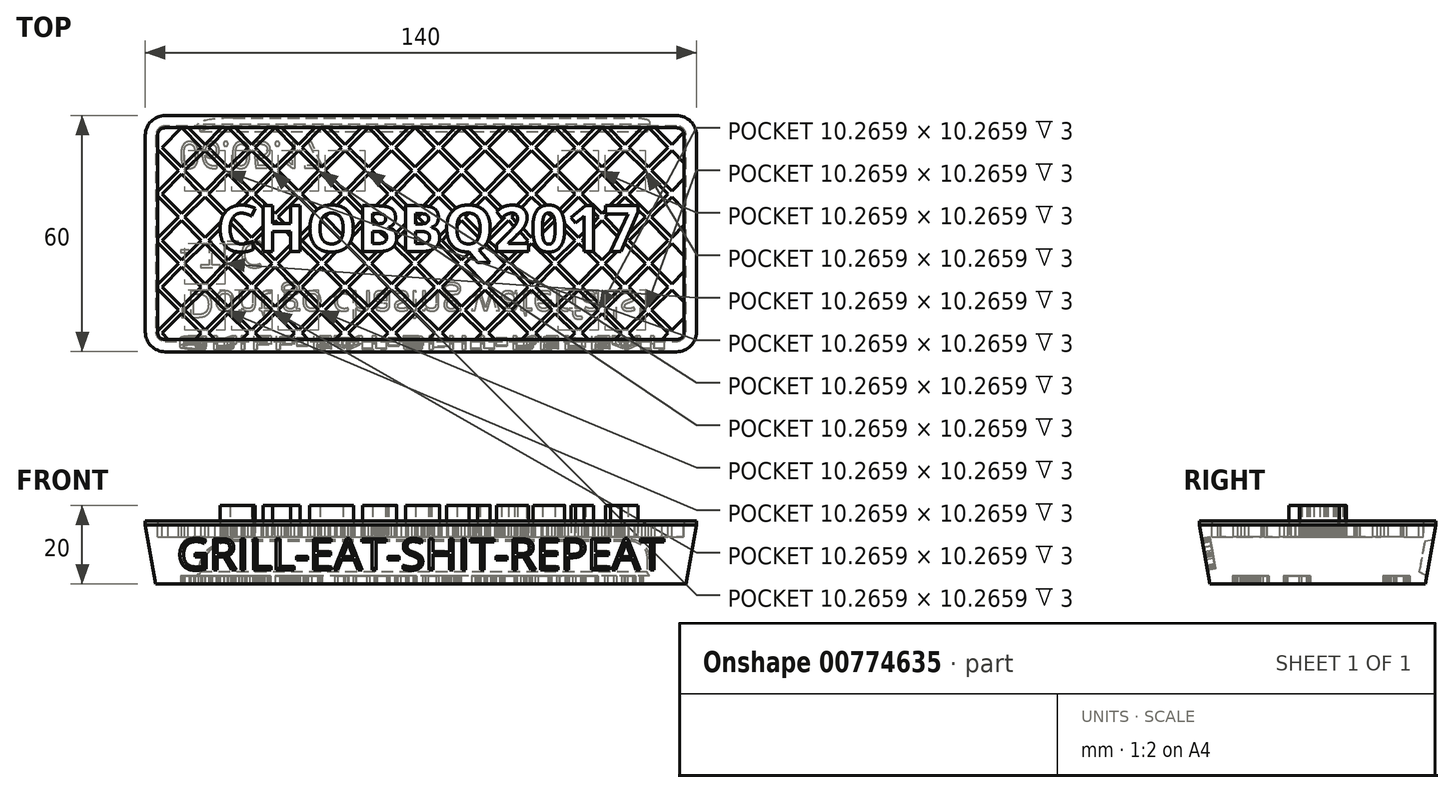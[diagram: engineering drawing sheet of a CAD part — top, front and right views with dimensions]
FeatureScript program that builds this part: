
annotation { "Feature Type Name" : "Feature", "Feature Type Description" : "" }
export const myFeature = defineFeature(function(context is Context, id is Id, definition is map)
    precondition{}
    {
        {
            var Q0;
            Q0=qCreatedBy(makeId("Top.planeOp"),FACE);
            var sketch = newSketch(context, id + "F0", { "sketchPlane" : qUnion([Q0])});
            skText(sketch, "E0", { "text": "CHOBBQ2017", "fontName": "NotoSans-Bold.ttf"});
            const initialGuessF0  = {"E0": [-0.0529, 0, 1, 0, 0.0117]};
            skSetInitialGuess(sketch, initialGuessF0);
            skSolve(sketch);
        }
        {
            var Q0;
            Q0=qCreatedBy(makeId("Top.planeOp"),FACE);
            var sketch = newSketch(context, id + "F1", { "sketchPlane" : qUnion([Q0])});
            skLineSegment(sketch, "E1.bottom", {"start": v(-65.96, 34.5) * mm, "end": v(64.04, 34.5) * mm});
            skLineSegment(sketch, "E1.top", {"start": v(-65.96, -25.5) * mm, "end": v(64.04, -25.5) * mm});
            skLineSegment(sketch, "E1.left", {"start": v(-70.96, 29.5) * mm, "end": v(-70.96, -20.5) * mm});
            skLineSegment(sketch, "E1.right", {"start": v(69.04, 29.5) * mm, "end": v(69.04, -20.5) * mm});
            skPoint(sketch, "E2.visualSharp", {"position": v(-70.96, 34.5) * mm});
            skArc(sketch, "E2.filletArc", {"start": v(-65.96, 34.5) * mm, "mid": v(-69.5, 33.04) * mm, "end": v(-70.96, 29.5) * mm});
            skPoint(sketch, "E3.visualSharp", {"position": v(-70.96, -25.5) * mm});
            skArc(sketch, "E3.filletArc", {"start": v(-70.96, -20.5) * mm, "mid": v(-69.5, -24.03) * mm, "end": v(-65.96, -25.5) * mm});
            skPoint(sketch, "E4.visualSharp", {"position": v(69.04, -25.5) * mm});
            skArc(sketch, "E4.filletArc", {"start": v(64.04, -25.5) * mm, "mid": v(67.58, -24.03) * mm, "end": v(69.04, -20.5) * mm});
            skPoint(sketch, "E5.visualSharp", {"position": v(69.04, 34.5) * mm});
            skArc(sketch, "E5.filletArc", {"start": v(69.04, 29.5) * mm, "mid": v(67.58, 33.04) * mm, "end": v(64.04, 34.5) * mm});
            skSolve(sketch);
        }
        {
            var Q0;
            Q0=makeQuery(id+"F1.imprint","IMPRINT",FACE,{"disambiguationData":[TD([[makeQuery(id+"F1.imprint","IMPRINT",EDGE,{"derivedFrom":sQuery(id+"F1.wireOp",EDGE,"E1.bottom")}),-1.0]])]});
            extrude(context, id + "F2", {"entities" : qUnion([Q0]), "oppositeDirection" : true, "depth" : 15 * mm, "offsetDistance" : 25 * mm, "hasDraft" : true, "draftAngle" : 10 * degree, "draftPullDirection" : true});
        }
        {
            var Q0;
            Q0=makeQuery(id+"F2.opExtrude","CAP_FACE",FACE,{"disambiguationData":[OSD([sQuery(id+"F1.wireOp",EDGE,"E1.bottom"),sQuery(id+"F1.wireOp",EDGE,"E1.top"),sQuery(id+"F1.wireOp",EDGE,"E1.left"),sQuery(id+"F1.wireOp",EDGE,"E1.right"),sQuery(id+"F1.wireOp",EDGE,"E2.filletArc"),sQuery(id+"F1.wireOp",EDGE,"E3.filletArc"),sQuery(id+"F1.wireOp",EDGE,"E4.filletArc"),sQuery(id+"F1.wireOp",EDGE,"E5.filletArc")])],"isStart":true});
            var sketch = newSketch(context, id + "F3", { "sketchPlane" : qUnion([Q0])});
            skArc(sketch, "E6.0", {"start": v(-65.96, 31.4) * mm, "mid": v(-67.3, 30.85) * mm, "end": v(-67.86, 29.5) * mm});
            skLineSegment(sketch, "E6.1", {"start": v(-67.86, 29.5) * mm, "end": v(-67.86, -20.5) * mm});
            skLineSegment(sketch, "E6.2", {"start": v(-65.96, 31.4) * mm, "end": v(64.04, 31.4) * mm});
            skArc(sketch, "E6.3", {"start": v(-67.86, -20.5) * mm, "mid": v(-67.3, -21.84) * mm, "end": v(-65.96, -22.4) * mm});
            skArc(sketch, "E6.4", {"start": v(65.94, 29.5) * mm, "mid": v(65.39, 30.85) * mm, "end": v(64.04, 31.4) * mm});
            skLineSegment(sketch, "E6.5", {"start": v(65.94, 29.5) * mm, "end": v(65.94, -20.5) * mm});
            skArc(sketch, "E6.6", {"start": v(64.04, -22.4) * mm, "mid": v(65.39, -21.84) * mm, "end": v(65.94, -20.5) * mm});
            skLineSegment(sketch, "E6.7", {"start": v(-65.96, -22.4) * mm, "end": v(64.04, -22.4) * mm});
            skSolve(sketch);
        }
        {
            var Q0;
            Q0=makeQuery(id+"F3.imprint","IMPRINT",FACE,{"disambiguationData":[TD([[makeQuery(id+"F3.imprint","IMPRINT",EDGE,{"derivedFrom":sQuery(id+"F3.wireOp",EDGE,"E6.0")}),-1.0]])]});
            extrude(context, id + "F4", {"entities" : qUnion([Q0]), "operationType" : NewBodyOperationType.ADD, "depth" : 1 * mm, "offsetDistance" : 25 * mm});
        }
        {
            var Q0;
            Q0=makeQuery(id+"F2.opExtrude","CAP_FACE",FACE,{"disambiguationData":[OSD([sQuery(id+"F1.wireOp",EDGE,"E1.bottom"),sQuery(id+"F1.wireOp",EDGE,"E1.top"),sQuery(id+"F1.wireOp",EDGE,"E1.left"),sQuery(id+"F1.wireOp",EDGE,"E1.right"),sQuery(id+"F1.wireOp",EDGE,"E2.filletArc"),sQuery(id+"F1.wireOp",EDGE,"E3.filletArc"),sQuery(id+"F1.wireOp",EDGE,"E4.filletArc"),sQuery(id+"F1.wireOp",EDGE,"E5.filletArc")])],"isStart":true});
            var sketch = newSketch(context, id + "F5", { "sketchPlane" : qUnion([Q0])});
            skLineSegment(sketch, "E7", {"start": v(-66.74, 26.4) * mm, "end": v(-61.74, 31.4) * mm});
            skLineSegment(sketch, "E8", {"start": v(-66.74, 26.4) * mm, "end": v(-61.74, 21.4) * mm});
            skLineSegment(sketch, "E9", {"start": v(-61.74, 21.4) * mm, "end": v(-56.74, 26.4) * mm});
            skLineSegment(sketch, "E10", {"start": v(-56.74, 26.4) * mm, "end": v(-61.74, 31.4) * mm});
            skLineSegment(sketch, "E11.0", {"start": v(-61.74, 19.7) * mm, "end": v(-55.04, 26.4) * mm});
            skLineSegment(sketch, "E11.1", {"start": v(-68.44, 26.4) * mm, "end": v(-61.74, 19.7) * mm});
            skLineSegment(sketch, "E11.2", {"start": v(-68.44, 26.4) * mm, "end": v(-61.74, 33.1) * mm});
            skLineSegment(sketch, "E11.3", {"start": v(-55.04, 26.4) * mm, "end": v(-61.74, 33.1) * mm});
            skLineSegment(sketch, "E12.0.1.0", {"start": v(-68.44, 14.6) * mm, "end": v(-61.74, 21.3) * mm});
            skLineSegment(sketch, "E12.0.1.1", {"start": v(-66.74, 14.6) * mm, "end": v(-61.74, 19.6) * mm});
            skLineSegment(sketch, "E12.0.1.2", {"start": v(-55.04, 14.6) * mm, "end": v(-61.74, 21.3) * mm});
            skLineSegment(sketch, "E12.0.1.3", {"start": v(-56.74, 14.6) * mm, "end": v(-61.74, 19.6) * mm});
            skLineSegment(sketch, "E12.0.1.4", {"start": v(-61.74, 7.9) * mm, "end": v(-55.04, 14.6) * mm});
            skLineSegment(sketch, "E12.0.1.5", {"start": v(-61.74, 9.6) * mm, "end": v(-56.74, 14.6) * mm});
            skLineSegment(sketch, "E12.0.1.6", {"start": v(-66.74, 14.6) * mm, "end": v(-61.74, 9.6) * mm});
            skLineSegment(sketch, "E12.0.1.7", {"start": v(-68.44, 14.6) * mm, "end": v(-61.74, 7.9) * mm});
            skLineSegment(sketch, "E12.0.2.0", {"start": v(-68.44, 2.8) * mm, "end": v(-61.74, 9.5) * mm});
            skLineSegment(sketch, "E12.0.2.1", {"start": v(-66.74, 2.8) * mm, "end": v(-61.74, 7.8) * mm});
            skLineSegment(sketch, "E12.0.2.2", {"start": v(-55.04, 2.8) * mm, "end": v(-61.74, 9.5) * mm});
            skLineSegment(sketch, "E12.0.2.3", {"start": v(-56.74, 2.8) * mm, "end": v(-61.74, 7.8) * mm});
            skLineSegment(sketch, "E12.0.2.4", {"start": v(-61.74, -3.9) * mm, "end": v(-55.04, 2.8) * mm});
            skLineSegment(sketch, "E12.0.2.5", {"start": v(-61.74, -2.2) * mm, "end": v(-56.74, 2.8) * mm});
            skLineSegment(sketch, "E12.0.2.6", {"start": v(-66.74, 2.8) * mm, "end": v(-61.74, -2.2) * mm});
            skLineSegment(sketch, "E12.0.2.7", {"start": v(-68.44, 2.8) * mm, "end": v(-61.74, -3.9) * mm});
            skLineSegment(sketch, "E12.0.3.0", {"start": v(-68.44, -9) * mm, "end": v(-61.74, -2.3) * mm});
            skLineSegment(sketch, "E12.0.3.1", {"start": v(-66.74, -9) * mm, "end": v(-61.74, -4) * mm});
            skLineSegment(sketch, "E12.0.3.2", {"start": v(-55.04, -9) * mm, "end": v(-61.74, -2.3) * mm});
            skLineSegment(sketch, "E12.0.3.3", {"start": v(-56.74, -9) * mm, "end": v(-61.74, -4) * mm});
            skLineSegment(sketch, "E12.0.3.4", {"start": v(-61.74, -15.7) * mm, "end": v(-55.04, -9) * mm});
            skLineSegment(sketch, "E12.0.3.5", {"start": v(-61.74, -14) * mm, "end": v(-56.74, -9) * mm});
            skLineSegment(sketch, "E12.0.3.6", {"start": v(-66.74, -9) * mm, "end": v(-61.74, -14) * mm});
            skLineSegment(sketch, "E12.0.3.7", {"start": v(-68.44, -9) * mm, "end": v(-61.74, -15.7) * mm});
            skLineSegment(sketch, "E12.0.4.0", {"start": v(-68.44, -20.8) * mm, "end": v(-61.74, -14.1) * mm});
            skLineSegment(sketch, "E12.0.4.1", {"start": v(-66.74, -20.8) * mm, "end": v(-61.74, -15.8) * mm});
            skLineSegment(sketch, "E12.0.4.2", {"start": v(-55.04, -20.8) * mm, "end": v(-61.74, -14.1) * mm});
            skLineSegment(sketch, "E12.0.4.3", {"start": v(-56.74, -20.8) * mm, "end": v(-61.74, -15.8) * mm});
            skLineSegment(sketch, "E12.0.4.4", {"start": v(-61.74, -27.5) * mm, "end": v(-55.04, -20.8) * mm});
            skLineSegment(sketch, "E12.0.4.5", {"start": v(-61.74, -25.8) * mm, "end": v(-56.74, -20.8) * mm});
            skLineSegment(sketch, "E12.0.4.6", {"start": v(-66.74, -20.8) * mm, "end": v(-61.74, -25.8) * mm});
            skLineSegment(sketch, "E12.0.4.7", {"start": v(-68.44, -20.8) * mm, "end": v(-61.74, -27.5) * mm});
            skLineSegment(sketch, "E12.1.0.0", {"start": v(-56.58, 26.4) * mm, "end": v(-49.88, 33.1) * mm});
            skLineSegment(sketch, "E12.1.0.1", {"start": v(-54.88, 26.4) * mm, "end": v(-49.88, 31.4) * mm});
            skLineSegment(sketch, "E12.1.0.2", {"start": v(-43.18, 26.4) * mm, "end": v(-49.88, 33.1) * mm});
            skLineSegment(sketch, "E12.1.0.3", {"start": v(-44.88, 26.4) * mm, "end": v(-49.88, 31.4) * mm});
            skLineSegment(sketch, "E12.1.0.4", {"start": v(-49.88, 19.7) * mm, "end": v(-43.18, 26.4) * mm});
            skLineSegment(sketch, "E12.1.0.5", {"start": v(-49.88, 21.4) * mm, "end": v(-44.88, 26.4) * mm});
            skLineSegment(sketch, "E12.1.0.6", {"start": v(-54.88, 26.4) * mm, "end": v(-49.88, 21.4) * mm});
            skLineSegment(sketch, "E12.1.0.7", {"start": v(-56.58, 26.4) * mm, "end": v(-49.88, 19.7) * mm});
            skLineSegment(sketch, "E12.1.1.0", {"start": v(-56.58, 14.6) * mm, "end": v(-49.88, 21.3) * mm});
            skLineSegment(sketch, "E12.1.1.1", {"start": v(-54.88, 14.6) * mm, "end": v(-49.88, 19.6) * mm});
            skLineSegment(sketch, "E12.1.1.2", {"start": v(-43.18, 14.6) * mm, "end": v(-49.88, 21.3) * mm});
            skLineSegment(sketch, "E12.1.1.3", {"start": v(-44.88, 14.6) * mm, "end": v(-49.88, 19.6) * mm});
            skLineSegment(sketch, "E12.1.1.4", {"start": v(-49.88, 7.9) * mm, "end": v(-43.18, 14.6) * mm});
            skLineSegment(sketch, "E12.1.1.5", {"start": v(-49.88, 9.6) * mm, "end": v(-44.88, 14.6) * mm});
            skLineSegment(sketch, "E12.1.1.6", {"start": v(-54.88, 14.6) * mm, "end": v(-49.88, 9.6) * mm});
            skLineSegment(sketch, "E12.1.1.7", {"start": v(-56.58, 14.6) * mm, "end": v(-49.88, 7.9) * mm});
            skLineSegment(sketch, "E12.1.2.0", {"start": v(-56.58, 2.8) * mm, "end": v(-49.88, 9.5) * mm});
            skLineSegment(sketch, "E12.1.2.1", {"start": v(-54.88, 2.8) * mm, "end": v(-49.88, 7.8) * mm});
            skLineSegment(sketch, "E12.1.2.2", {"start": v(-43.18, 2.8) * mm, "end": v(-49.88, 9.5) * mm});
            skLineSegment(sketch, "E12.1.2.3", {"start": v(-44.88, 2.8) * mm, "end": v(-49.88, 7.8) * mm});
            skLineSegment(sketch, "E12.1.2.4", {"start": v(-49.88, -3.9) * mm, "end": v(-43.18, 2.8) * mm});
            skLineSegment(sketch, "E12.1.2.5", {"start": v(-49.88, -2.2) * mm, "end": v(-44.88, 2.8) * mm});
            skLineSegment(sketch, "E12.1.2.6", {"start": v(-54.88, 2.8) * mm, "end": v(-49.88, -2.2) * mm});
            skLineSegment(sketch, "E12.1.2.7", {"start": v(-56.58, 2.8) * mm, "end": v(-49.88, -3.9) * mm});
            skLineSegment(sketch, "E12.1.3.0", {"start": v(-56.58, -9) * mm, "end": v(-49.88, -2.3) * mm});
            skLineSegment(sketch, "E12.1.3.1", {"start": v(-54.88, -9) * mm, "end": v(-49.88, -4) * mm});
            skLineSegment(sketch, "E12.1.3.2", {"start": v(-43.18, -9) * mm, "end": v(-49.88, -2.3) * mm});
            skLineSegment(sketch, "E12.1.3.3", {"start": v(-44.88, -9) * mm, "end": v(-49.88, -4) * mm});
            skLineSegment(sketch, "E12.1.3.4", {"start": v(-49.88, -15.7) * mm, "end": v(-43.18, -9) * mm});
            skLineSegment(sketch, "E12.1.3.5", {"start": v(-49.88, -14) * mm, "end": v(-44.88, -9) * mm});
            skLineSegment(sketch, "E12.1.3.6", {"start": v(-54.88, -9) * mm, "end": v(-49.88, -14) * mm});
            skLineSegment(sketch, "E12.1.3.7", {"start": v(-56.58, -9) * mm, "end": v(-49.88, -15.7) * mm});
            skLineSegment(sketch, "E12.1.4.0", {"start": v(-56.58, -20.8) * mm, "end": v(-49.88, -14.1) * mm});
            skLineSegment(sketch, "E12.1.4.1", {"start": v(-54.88, -20.8) * mm, "end": v(-49.88, -15.8) * mm});
            skLineSegment(sketch, "E12.1.4.2", {"start": v(-43.18, -20.8) * mm, "end": v(-49.88, -14.1) * mm});
            skLineSegment(sketch, "E12.1.4.3", {"start": v(-44.88, -20.8) * mm, "end": v(-49.88, -15.8) * mm});
            skLineSegment(sketch, "E12.1.4.4", {"start": v(-49.88, -27.5) * mm, "end": v(-43.18, -20.8) * mm});
            skLineSegment(sketch, "E12.1.4.5", {"start": v(-49.88, -25.8) * mm, "end": v(-44.88, -20.8) * mm});
            skLineSegment(sketch, "E12.1.4.6", {"start": v(-54.88, -20.8) * mm, "end": v(-49.88, -25.8) * mm});
            skLineSegment(sketch, "E12.1.4.7", {"start": v(-56.58, -20.8) * mm, "end": v(-49.88, -27.5) * mm});
            skLineSegment(sketch, "E12.2.0.0", {"start": v(-44.72, 26.4) * mm, "end": v(-38.02, 33.1) * mm});
            skLineSegment(sketch, "E12.2.0.1", {"start": v(-43.02, 26.4) * mm, "end": v(-38.02, 31.4) * mm});
            skLineSegment(sketch, "E12.2.0.2", {"start": v(-31.32, 26.4) * mm, "end": v(-38.02, 33.1) * mm});
            skLineSegment(sketch, "E12.2.0.3", {"start": v(-33.02, 26.4) * mm, "end": v(-38.02, 31.4) * mm});
            skLineSegment(sketch, "E12.2.0.4", {"start": v(-38.02, 19.7) * mm, "end": v(-31.32, 26.4) * mm});
            skLineSegment(sketch, "E12.2.0.5", {"start": v(-38.02, 21.4) * mm, "end": v(-33.02, 26.4) * mm});
            skLineSegment(sketch, "E12.2.0.6", {"start": v(-43.02, 26.4) * mm, "end": v(-38.02, 21.4) * mm});
            skLineSegment(sketch, "E12.2.0.7", {"start": v(-44.72, 26.4) * mm, "end": v(-38.02, 19.7) * mm});
            skLineSegment(sketch, "E12.2.1.0", {"start": v(-44.72, 14.6) * mm, "end": v(-38.02, 21.3) * mm});
            skLineSegment(sketch, "E12.2.1.1", {"start": v(-43.02, 14.6) * mm, "end": v(-38.02, 19.6) * mm});
            skLineSegment(sketch, "E12.2.1.2", {"start": v(-31.32, 14.6) * mm, "end": v(-38.02, 21.3) * mm});
            skLineSegment(sketch, "E12.2.1.3", {"start": v(-33.02, 14.6) * mm, "end": v(-38.02, 19.6) * mm});
            skLineSegment(sketch, "E12.2.1.4", {"start": v(-38.02, 7.9) * mm, "end": v(-31.32, 14.6) * mm});
            skLineSegment(sketch, "E12.2.1.5", {"start": v(-38.02, 9.6) * mm, "end": v(-33.02, 14.6) * mm});
            skLineSegment(sketch, "E12.2.1.6", {"start": v(-43.02, 14.6) * mm, "end": v(-38.02, 9.6) * mm});
            skLineSegment(sketch, "E12.2.1.7", {"start": v(-44.72, 14.6) * mm, "end": v(-38.02, 7.9) * mm});
            skLineSegment(sketch, "E12.2.2.0", {"start": v(-44.72, 2.8) * mm, "end": v(-38.02, 9.5) * mm});
            skLineSegment(sketch, "E12.2.2.1", {"start": v(-43.02, 2.8) * mm, "end": v(-38.02, 7.8) * mm});
            skLineSegment(sketch, "E12.2.2.2", {"start": v(-31.32, 2.8) * mm, "end": v(-38.02, 9.5) * mm});
            skLineSegment(sketch, "E12.2.2.3", {"start": v(-33.02, 2.8) * mm, "end": v(-38.02, 7.8) * mm});
            skLineSegment(sketch, "E12.2.2.4", {"start": v(-38.02, -3.9) * mm, "end": v(-31.32, 2.8) * mm});
            skLineSegment(sketch, "E12.2.2.5", {"start": v(-38.02, -2.2) * mm, "end": v(-33.02, 2.8) * mm});
            skLineSegment(sketch, "E12.2.2.6", {"start": v(-43.02, 2.8) * mm, "end": v(-38.02, -2.2) * mm});
            skLineSegment(sketch, "E12.2.2.7", {"start": v(-44.72, 2.8) * mm, "end": v(-38.02, -3.9) * mm});
            skLineSegment(sketch, "E12.2.3.0", {"start": v(-44.72, -9) * mm, "end": v(-38.02, -2.3) * mm});
            skLineSegment(sketch, "E12.2.3.1", {"start": v(-43.02, -9) * mm, "end": v(-38.02, -4) * mm});
            skLineSegment(sketch, "E12.2.3.2", {"start": v(-31.32, -9) * mm, "end": v(-38.02, -2.3) * mm});
            skLineSegment(sketch, "E12.2.3.3", {"start": v(-33.02, -9) * mm, "end": v(-38.02, -4) * mm});
            skLineSegment(sketch, "E12.2.3.4", {"start": v(-38.02, -15.7) * mm, "end": v(-31.32, -9) * mm});
            skLineSegment(sketch, "E12.2.3.5", {"start": v(-38.02, -14) * mm, "end": v(-33.02, -9) * mm});
            skLineSegment(sketch, "E12.2.3.6", {"start": v(-43.02, -9) * mm, "end": v(-38.02, -14) * mm});
            skLineSegment(sketch, "E12.2.3.7", {"start": v(-44.72, -9) * mm, "end": v(-38.02, -15.7) * mm});
            skLineSegment(sketch, "E12.2.4.0", {"start": v(-44.72, -20.8) * mm, "end": v(-38.02, -14.1) * mm});
            skLineSegment(sketch, "E12.2.4.1", {"start": v(-43.02, -20.8) * mm, "end": v(-38.02, -15.8) * mm});
            skLineSegment(sketch, "E12.2.4.2", {"start": v(-31.32, -20.8) * mm, "end": v(-38.02, -14.1) * mm});
            skLineSegment(sketch, "E12.2.4.3", {"start": v(-33.02, -20.8) * mm, "end": v(-38.02, -15.8) * mm});
            skLineSegment(sketch, "E12.2.4.4", {"start": v(-38.02, -27.5) * mm, "end": v(-31.32, -20.8) * mm});
            skLineSegment(sketch, "E12.2.4.5", {"start": v(-38.02, -25.8) * mm, "end": v(-33.02, -20.8) * mm});
            skLineSegment(sketch, "E12.2.4.6", {"start": v(-43.02, -20.8) * mm, "end": v(-38.02, -25.8) * mm});
            skLineSegment(sketch, "E12.2.4.7", {"start": v(-44.72, -20.8) * mm, "end": v(-38.02, -27.5) * mm});
            skLineSegment(sketch, "E12.3.0.0", {"start": v(-32.86, 26.4) * mm, "end": v(-26.16, 33.1) * mm});
            skLineSegment(sketch, "E12.3.0.1", {"start": v(-31.16, 26.4) * mm, "end": v(-26.16, 31.4) * mm});
            skLineSegment(sketch, "E12.3.0.2", {"start": v(-19.46, 26.4) * mm, "end": v(-26.16, 33.1) * mm});
            skLineSegment(sketch, "E12.3.0.3", {"start": v(-21.16, 26.4) * mm, "end": v(-26.16, 31.4) * mm});
            skLineSegment(sketch, "E12.3.0.4", {"start": v(-26.16, 19.7) * mm, "end": v(-19.46, 26.4) * mm});
            skLineSegment(sketch, "E12.3.0.5", {"start": v(-26.16, 21.4) * mm, "end": v(-21.16, 26.4) * mm});
            skLineSegment(sketch, "E12.3.0.6", {"start": v(-31.16, 26.4) * mm, "end": v(-26.16, 21.4) * mm});
            skLineSegment(sketch, "E12.3.0.7", {"start": v(-32.86, 26.4) * mm, "end": v(-26.16, 19.7) * mm});
            skLineSegment(sketch, "E12.3.1.0", {"start": v(-32.86, 14.6) * mm, "end": v(-26.16, 21.3) * mm});
            skLineSegment(sketch, "E12.3.1.1", {"start": v(-31.16, 14.6) * mm, "end": v(-26.16, 19.6) * mm});
            skLineSegment(sketch, "E12.3.1.2", {"start": v(-19.46, 14.6) * mm, "end": v(-26.16, 21.3) * mm});
            skLineSegment(sketch, "E12.3.1.3", {"start": v(-21.16, 14.6) * mm, "end": v(-26.16, 19.6) * mm});
            skLineSegment(sketch, "E12.3.1.4", {"start": v(-26.16, 7.9) * mm, "end": v(-19.46, 14.6) * mm});
            skLineSegment(sketch, "E12.3.1.5", {"start": v(-26.16, 9.6) * mm, "end": v(-21.16, 14.6) * mm});
            skLineSegment(sketch, "E12.3.1.6", {"start": v(-31.16, 14.6) * mm, "end": v(-26.16, 9.6) * mm});
            skLineSegment(sketch, "E12.3.1.7", {"start": v(-32.86, 14.6) * mm, "end": v(-26.16, 7.9) * mm});
            skLineSegment(sketch, "E12.3.2.0", {"start": v(-32.86, 2.8) * mm, "end": v(-26.16, 9.5) * mm});
            skLineSegment(sketch, "E12.3.2.1", {"start": v(-31.16, 2.8) * mm, "end": v(-26.16, 7.8) * mm});
            skLineSegment(sketch, "E12.3.2.2", {"start": v(-19.46, 2.8) * mm, "end": v(-26.16, 9.5) * mm});
            skLineSegment(sketch, "E12.3.2.3", {"start": v(-21.16, 2.8) * mm, "end": v(-26.16, 7.8) * mm});
            skLineSegment(sketch, "E12.3.2.4", {"start": v(-26.16, -3.9) * mm, "end": v(-19.46, 2.8) * mm});
            skLineSegment(sketch, "E12.3.2.5", {"start": v(-26.16, -2.2) * mm, "end": v(-21.16, 2.8) * mm});
            skLineSegment(sketch, "E12.3.2.6", {"start": v(-31.16, 2.8) * mm, "end": v(-26.16, -2.2) * mm});
            skLineSegment(sketch, "E12.3.2.7", {"start": v(-32.86, 2.8) * mm, "end": v(-26.16, -3.9) * mm});
            skLineSegment(sketch, "E12.3.3.0", {"start": v(-32.86, -9) * mm, "end": v(-26.16, -2.3) * mm});
            skLineSegment(sketch, "E12.3.3.1", {"start": v(-31.16, -9) * mm, "end": v(-26.16, -4) * mm});
            skLineSegment(sketch, "E12.3.3.2", {"start": v(-19.46, -9) * mm, "end": v(-26.16, -2.3) * mm});
            skLineSegment(sketch, "E12.3.3.3", {"start": v(-21.16, -9) * mm, "end": v(-26.16, -4) * mm});
            skLineSegment(sketch, "E12.3.3.4", {"start": v(-26.16, -15.7) * mm, "end": v(-19.46, -9) * mm});
            skLineSegment(sketch, "E12.3.3.5", {"start": v(-26.16, -14) * mm, "end": v(-21.16, -9) * mm});
            skLineSegment(sketch, "E12.3.3.6", {"start": v(-31.16, -9) * mm, "end": v(-26.16, -14) * mm});
            skLineSegment(sketch, "E12.3.3.7", {"start": v(-32.86, -9) * mm, "end": v(-26.16, -15.7) * mm});
            skLineSegment(sketch, "E12.3.4.0", {"start": v(-32.86, -20.8) * mm, "end": v(-26.16, -14.1) * mm});
            skLineSegment(sketch, "E12.3.4.1", {"start": v(-31.16, -20.8) * mm, "end": v(-26.16, -15.8) * mm});
            skLineSegment(sketch, "E12.3.4.2", {"start": v(-19.46, -20.8) * mm, "end": v(-26.16, -14.1) * mm});
            skLineSegment(sketch, "E12.3.4.3", {"start": v(-21.16, -20.8) * mm, "end": v(-26.16, -15.8) * mm});
            skLineSegment(sketch, "E12.3.4.4", {"start": v(-26.16, -27.5) * mm, "end": v(-19.46, -20.8) * mm});
            skLineSegment(sketch, "E12.3.4.5", {"start": v(-26.16, -25.8) * mm, "end": v(-21.16, -20.8) * mm});
            skLineSegment(sketch, "E12.3.4.6", {"start": v(-31.16, -20.8) * mm, "end": v(-26.16, -25.8) * mm});
            skLineSegment(sketch, "E12.3.4.7", {"start": v(-32.86, -20.8) * mm, "end": v(-26.16, -27.5) * mm});
            skLineSegment(sketch, "E12.4.0.0", {"start": v(-21, 26.4) * mm, "end": v(-14.3, 33.1) * mm});
            skLineSegment(sketch, "E12.4.0.1", {"start": v(-19.3, 26.4) * mm, "end": v(-14.3, 31.4) * mm});
            skLineSegment(sketch, "E12.4.0.2", {"start": v(-7.6, 26.4) * mm, "end": v(-14.3, 33.1) * mm});
            skLineSegment(sketch, "E12.4.0.3", {"start": v(-9.3, 26.4) * mm, "end": v(-14.3, 31.4) * mm});
            skLineSegment(sketch, "E12.4.0.4", {"start": v(-14.3, 19.7) * mm, "end": v(-7.6, 26.4) * mm});
            skLineSegment(sketch, "E12.4.0.5", {"start": v(-14.3, 21.4) * mm, "end": v(-9.3, 26.4) * mm});
            skLineSegment(sketch, "E12.4.0.6", {"start": v(-19.3, 26.4) * mm, "end": v(-14.3, 21.4) * mm});
            skLineSegment(sketch, "E12.4.0.7", {"start": v(-21, 26.4) * mm, "end": v(-14.3, 19.7) * mm});
            skLineSegment(sketch, "E12.4.1.0", {"start": v(-21, 14.6) * mm, "end": v(-14.3, 21.3) * mm});
            skLineSegment(sketch, "E12.4.1.1", {"start": v(-19.3, 14.6) * mm, "end": v(-14.3, 19.6) * mm});
            skLineSegment(sketch, "E12.4.1.2", {"start": v(-7.6, 14.6) * mm, "end": v(-14.3, 21.3) * mm});
            skLineSegment(sketch, "E12.4.1.3", {"start": v(-9.3, 14.6) * mm, "end": v(-14.3, 19.6) * mm});
            skLineSegment(sketch, "E12.4.1.4", {"start": v(-14.3, 7.9) * mm, "end": v(-7.6, 14.6) * mm});
            skLineSegment(sketch, "E12.4.1.5", {"start": v(-14.3, 9.6) * mm, "end": v(-9.3, 14.6) * mm});
            skLineSegment(sketch, "E12.4.1.6", {"start": v(-19.3, 14.6) * mm, "end": v(-14.3, 9.6) * mm});
            skLineSegment(sketch, "E12.4.1.7", {"start": v(-21, 14.6) * mm, "end": v(-14.3, 7.9) * mm});
            skLineSegment(sketch, "E12.4.2.0", {"start": v(-21, 2.8) * mm, "end": v(-14.3, 9.5) * mm});
            skLineSegment(sketch, "E12.4.2.1", {"start": v(-19.3, 2.8) * mm, "end": v(-14.3, 7.8) * mm});
            skLineSegment(sketch, "E12.4.2.2", {"start": v(-7.6, 2.8) * mm, "end": v(-14.3, 9.5) * mm});
            skLineSegment(sketch, "E12.4.2.3", {"start": v(-9.3, 2.8) * mm, "end": v(-14.3, 7.8) * mm});
            skLineSegment(sketch, "E12.4.2.4", {"start": v(-14.3, -3.9) * mm, "end": v(-7.6, 2.8) * mm});
            skLineSegment(sketch, "E12.4.2.5", {"start": v(-14.3, -2.2) * mm, "end": v(-9.3, 2.8) * mm});
            skLineSegment(sketch, "E12.4.2.6", {"start": v(-19.3, 2.8) * mm, "end": v(-14.3, -2.2) * mm});
            skLineSegment(sketch, "E12.4.2.7", {"start": v(-21, 2.8) * mm, "end": v(-14.3, -3.9) * mm});
            skLineSegment(sketch, "E12.4.3.0", {"start": v(-21, -9) * mm, "end": v(-14.3, -2.3) * mm});
            skLineSegment(sketch, "E12.4.3.1", {"start": v(-19.3, -9) * mm, "end": v(-14.3, -4) * mm});
            skLineSegment(sketch, "E12.4.3.2", {"start": v(-7.6, -9) * mm, "end": v(-14.3, -2.3) * mm});
            skLineSegment(sketch, "E12.4.3.3", {"start": v(-9.3, -9) * mm, "end": v(-14.3, -4) * mm});
            skLineSegment(sketch, "E12.4.3.4", {"start": v(-14.3, -15.7) * mm, "end": v(-7.6, -9) * mm});
            skLineSegment(sketch, "E12.4.3.5", {"start": v(-14.3, -14) * mm, "end": v(-9.3, -9) * mm});
            skLineSegment(sketch, "E12.4.3.6", {"start": v(-19.3, -9) * mm, "end": v(-14.3, -14) * mm});
            skLineSegment(sketch, "E12.4.3.7", {"start": v(-21, -9) * mm, "end": v(-14.3, -15.7) * mm});
            skLineSegment(sketch, "E12.4.4.0", {"start": v(-21, -20.8) * mm, "end": v(-14.3, -14.1) * mm});
            skLineSegment(sketch, "E12.4.4.1", {"start": v(-19.3, -20.8) * mm, "end": v(-14.3, -15.8) * mm});
            skLineSegment(sketch, "E12.4.4.2", {"start": v(-7.6, -20.8) * mm, "end": v(-14.3, -14.1) * mm});
            skLineSegment(sketch, "E12.4.4.3", {"start": v(-9.3, -20.8) * mm, "end": v(-14.3, -15.8) * mm});
            skLineSegment(sketch, "E12.4.4.4", {"start": v(-14.3, -27.5) * mm, "end": v(-7.6, -20.8) * mm});
            skLineSegment(sketch, "E12.4.4.5", {"start": v(-14.3, -25.8) * mm, "end": v(-9.3, -20.8) * mm});
            skLineSegment(sketch, "E12.4.4.6", {"start": v(-19.3, -20.8) * mm, "end": v(-14.3, -25.8) * mm});
            skLineSegment(sketch, "E12.4.4.7", {"start": v(-21, -20.8) * mm, "end": v(-14.3, -27.5) * mm});
            skLineSegment(sketch, "E12.5.0.0", {"start": v(-9.14, 26.4) * mm, "end": v(-2.44, 33.1) * mm});
            skLineSegment(sketch, "E12.5.0.1", {"start": v(-7.44, 26.4) * mm, "end": v(-2.44, 31.4) * mm});
            skLineSegment(sketch, "E12.5.0.2", {"start": v(4.26, 26.4) * mm, "end": v(-2.44, 33.1) * mm});
            skLineSegment(sketch, "E12.5.0.3", {"start": v(2.56, 26.4) * mm, "end": v(-2.44, 31.4) * mm});
            skLineSegment(sketch, "E12.5.0.4", {"start": v(-2.44, 19.7) * mm, "end": v(4.26, 26.4) * mm});
            skLineSegment(sketch, "E12.5.0.5", {"start": v(-2.44, 21.4) * mm, "end": v(2.56, 26.4) * mm});
            skLineSegment(sketch, "E12.5.0.6", {"start": v(-7.44, 26.4) * mm, "end": v(-2.44, 21.4) * mm});
            skLineSegment(sketch, "E12.5.0.7", {"start": v(-9.14, 26.4) * mm, "end": v(-2.44, 19.7) * mm});
            skLineSegment(sketch, "E12.5.1.0", {"start": v(-9.14, 14.6) * mm, "end": v(-2.44, 21.3) * mm});
            skLineSegment(sketch, "E12.5.1.1", {"start": v(-7.44, 14.6) * mm, "end": v(-2.44, 19.6) * mm});
            skLineSegment(sketch, "E12.5.1.2", {"start": v(4.26, 14.6) * mm, "end": v(-2.44, 21.3) * mm});
            skLineSegment(sketch, "E12.5.1.3", {"start": v(2.56, 14.6) * mm, "end": v(-2.44, 19.6) * mm});
            skLineSegment(sketch, "E12.5.1.4", {"start": v(-2.44, 7.9) * mm, "end": v(4.26, 14.6) * mm});
            skLineSegment(sketch, "E12.5.1.5", {"start": v(-2.44, 9.6) * mm, "end": v(2.56, 14.6) * mm});
            skLineSegment(sketch, "E12.5.1.6", {"start": v(-7.44, 14.6) * mm, "end": v(-2.44, 9.6) * mm});
            skLineSegment(sketch, "E12.5.1.7", {"start": v(-9.14, 14.6) * mm, "end": v(-2.44, 7.9) * mm});
            skLineSegment(sketch, "E12.5.2.0", {"start": v(-9.14, 2.8) * mm, "end": v(-2.44, 9.5) * mm});
            skLineSegment(sketch, "E12.5.2.1", {"start": v(-7.44, 2.8) * mm, "end": v(-2.44, 7.8) * mm});
            skLineSegment(sketch, "E12.5.2.2", {"start": v(4.26, 2.8) * mm, "end": v(-2.44, 9.5) * mm});
            skLineSegment(sketch, "E12.5.2.3", {"start": v(2.56, 2.8) * mm, "end": v(-2.44, 7.8) * mm});
            skLineSegment(sketch, "E12.5.2.4", {"start": v(-2.44, -3.9) * mm, "end": v(4.26, 2.8) * mm});
            skLineSegment(sketch, "E12.5.2.5", {"start": v(-2.44, -2.2) * mm, "end": v(2.56, 2.8) * mm});
            skLineSegment(sketch, "E12.5.2.6", {"start": v(-7.44, 2.8) * mm, "end": v(-2.44, -2.2) * mm});
            skLineSegment(sketch, "E12.5.2.7", {"start": v(-9.14, 2.8) * mm, "end": v(-2.44, -3.9) * mm});
            skLineSegment(sketch, "E12.5.3.0", {"start": v(-9.14, -9) * mm, "end": v(-2.44, -2.3) * mm});
            skLineSegment(sketch, "E12.5.3.1", {"start": v(-7.44, -9) * mm, "end": v(-2.44, -4) * mm});
            skLineSegment(sketch, "E12.5.3.2", {"start": v(4.26, -9) * mm, "end": v(-2.44, -2.3) * mm});
            skLineSegment(sketch, "E12.5.3.3", {"start": v(2.56, -9) * mm, "end": v(-2.44, -4) * mm});
            skLineSegment(sketch, "E12.5.3.4", {"start": v(-2.44, -15.7) * mm, "end": v(4.26, -9) * mm});
            skLineSegment(sketch, "E12.5.3.5", {"start": v(-2.44, -14) * mm, "end": v(2.56, -9) * mm});
            skLineSegment(sketch, "E12.5.3.6", {"start": v(-7.44, -9) * mm, "end": v(-2.44, -14) * mm});
            skLineSegment(sketch, "E12.5.3.7", {"start": v(-9.14, -9) * mm, "end": v(-2.44, -15.7) * mm});
            skLineSegment(sketch, "E12.5.4.0", {"start": v(-9.14, -20.8) * mm, "end": v(-2.44, -14.1) * mm});
            skLineSegment(sketch, "E12.5.4.1", {"start": v(-7.44, -20.8) * mm, "end": v(-2.44, -15.8) * mm});
            skLineSegment(sketch, "E12.5.4.2", {"start": v(4.26, -20.8) * mm, "end": v(-2.44, -14.1) * mm});
            skLineSegment(sketch, "E12.5.4.3", {"start": v(2.56, -20.8) * mm, "end": v(-2.44, -15.8) * mm});
            skLineSegment(sketch, "E12.5.4.4", {"start": v(-2.44, -27.5) * mm, "end": v(4.26, -20.8) * mm});
            skLineSegment(sketch, "E12.5.4.5", {"start": v(-2.44, -25.8) * mm, "end": v(2.56, -20.8) * mm});
            skLineSegment(sketch, "E12.5.4.6", {"start": v(-7.44, -20.8) * mm, "end": v(-2.44, -25.8) * mm});
            skLineSegment(sketch, "E12.5.4.7", {"start": v(-9.14, -20.8) * mm, "end": v(-2.44, -27.5) * mm});
            skLineSegment(sketch, "E12.6.0.0", {"start": v(2.72, 26.4) * mm, "end": v(9.42, 33.1) * mm});
            skLineSegment(sketch, "E12.6.0.1", {"start": v(4.42, 26.4) * mm, "end": v(9.42, 31.4) * mm});
            skLineSegment(sketch, "E12.6.0.2", {"start": v(16.12, 26.4) * mm, "end": v(9.42, 33.1) * mm});
            skLineSegment(sketch, "E12.6.0.3", {"start": v(14.42, 26.4) * mm, "end": v(9.42, 31.4) * mm});
            skLineSegment(sketch, "E12.6.0.4", {"start": v(9.42, 19.7) * mm, "end": v(16.12, 26.4) * mm});
            skLineSegment(sketch, "E12.6.0.5", {"start": v(9.42, 21.4) * mm, "end": v(14.42, 26.4) * mm});
            skLineSegment(sketch, "E12.6.0.6", {"start": v(4.42, 26.4) * mm, "end": v(9.42, 21.4) * mm});
            skLineSegment(sketch, "E12.6.0.7", {"start": v(2.72, 26.4) * mm, "end": v(9.42, 19.7) * mm});
            skLineSegment(sketch, "E12.6.1.0", {"start": v(2.72, 14.6) * mm, "end": v(9.42, 21.3) * mm});
            skLineSegment(sketch, "E12.6.1.1", {"start": v(4.42, 14.6) * mm, "end": v(9.42, 19.6) * mm});
            skLineSegment(sketch, "E12.6.1.2", {"start": v(16.12, 14.6) * mm, "end": v(9.42, 21.3) * mm});
            skLineSegment(sketch, "E12.6.1.3", {"start": v(14.42, 14.6) * mm, "end": v(9.42, 19.6) * mm});
            skLineSegment(sketch, "E12.6.1.4", {"start": v(9.42, 7.9) * mm, "end": v(16.12, 14.6) * mm});
            skLineSegment(sketch, "E12.6.1.5", {"start": v(9.42, 9.6) * mm, "end": v(14.42, 14.6) * mm});
            skLineSegment(sketch, "E12.6.1.6", {"start": v(4.42, 14.6) * mm, "end": v(9.42, 9.6) * mm});
            skLineSegment(sketch, "E12.6.1.7", {"start": v(2.72, 14.6) * mm, "end": v(9.42, 7.9) * mm});
            skLineSegment(sketch, "E12.6.2.0", {"start": v(2.72, 2.8) * mm, "end": v(9.42, 9.5) * mm});
            skLineSegment(sketch, "E12.6.2.1", {"start": v(4.42, 2.8) * mm, "end": v(9.42, 7.8) * mm});
            skLineSegment(sketch, "E12.6.2.2", {"start": v(16.12, 2.8) * mm, "end": v(9.42, 9.5) * mm});
            skLineSegment(sketch, "E12.6.2.3", {"start": v(14.42, 2.8) * mm, "end": v(9.42, 7.8) * mm});
            skLineSegment(sketch, "E12.6.2.4", {"start": v(9.42, -3.9) * mm, "end": v(16.12, 2.8) * mm});
            skLineSegment(sketch, "E12.6.2.5", {"start": v(9.42, -2.2) * mm, "end": v(14.42, 2.8) * mm});
            skLineSegment(sketch, "E12.6.2.6", {"start": v(4.42, 2.8) * mm, "end": v(9.42, -2.2) * mm});
            skLineSegment(sketch, "E12.6.2.7", {"start": v(2.72, 2.8) * mm, "end": v(9.42, -3.9) * mm});
            skLineSegment(sketch, "E12.6.3.0", {"start": v(2.72, -9) * mm, "end": v(9.42, -2.3) * mm});
            skLineSegment(sketch, "E12.6.3.1", {"start": v(4.42, -9) * mm, "end": v(9.42, -4) * mm});
            skLineSegment(sketch, "E12.6.3.2", {"start": v(16.12, -9) * mm, "end": v(9.42, -2.3) * mm});
            skLineSegment(sketch, "E12.6.3.3", {"start": v(14.42, -9) * mm, "end": v(9.42, -4) * mm});
            skLineSegment(sketch, "E12.6.3.4", {"start": v(9.42, -15.7) * mm, "end": v(16.12, -9) * mm});
            skLineSegment(sketch, "E12.6.3.5", {"start": v(9.42, -14) * mm, "end": v(14.42, -9) * mm});
            skLineSegment(sketch, "E12.6.3.6", {"start": v(4.42, -9) * mm, "end": v(9.42, -14) * mm});
            skLineSegment(sketch, "E12.6.3.7", {"start": v(2.72, -9) * mm, "end": v(9.42, -15.7) * mm});
            skLineSegment(sketch, "E12.6.4.0", {"start": v(2.72, -20.8) * mm, "end": v(9.42, -14.1) * mm});
            skLineSegment(sketch, "E12.6.4.1", {"start": v(4.42, -20.8) * mm, "end": v(9.42, -15.8) * mm});
            skLineSegment(sketch, "E12.6.4.2", {"start": v(16.12, -20.8) * mm, "end": v(9.42, -14.1) * mm});
            skLineSegment(sketch, "E12.6.4.3", {"start": v(14.42, -20.8) * mm, "end": v(9.42, -15.8) * mm});
            skLineSegment(sketch, "E12.6.4.4", {"start": v(9.42, -27.5) * mm, "end": v(16.12, -20.8) * mm});
            skLineSegment(sketch, "E12.6.4.5", {"start": v(9.42, -25.8) * mm, "end": v(14.42, -20.8) * mm});
            skLineSegment(sketch, "E12.6.4.6", {"start": v(4.42, -20.8) * mm, "end": v(9.42, -25.8) * mm});
            skLineSegment(sketch, "E12.6.4.7", {"start": v(2.72, -20.8) * mm, "end": v(9.42, -27.5) * mm});
            skLineSegment(sketch, "E12.7.0.0", {"start": v(14.58, 26.4) * mm, "end": v(21.28, 33.1) * mm});
            skLineSegment(sketch, "E12.7.0.1", {"start": v(16.28, 26.4) * mm, "end": v(21.28, 31.4) * mm});
            skLineSegment(sketch, "E12.7.0.2", {"start": v(27.98, 26.4) * mm, "end": v(21.28, 33.1) * mm});
            skLineSegment(sketch, "E12.7.0.3", {"start": v(26.28, 26.4) * mm, "end": v(21.28, 31.4) * mm});
            skLineSegment(sketch, "E12.7.0.4", {"start": v(21.28, 19.7) * mm, "end": v(27.98, 26.4) * mm});
            skLineSegment(sketch, "E12.7.0.5", {"start": v(21.28, 21.4) * mm, "end": v(26.28, 26.4) * mm});
            skLineSegment(sketch, "E12.7.0.6", {"start": v(16.28, 26.4) * mm, "end": v(21.28, 21.4) * mm});
            skLineSegment(sketch, "E12.7.0.7", {"start": v(14.58, 26.4) * mm, "end": v(21.28, 19.7) * mm});
            skLineSegment(sketch, "E12.7.1.0", {"start": v(14.58, 14.6) * mm, "end": v(21.28, 21.3) * mm});
            skLineSegment(sketch, "E12.7.1.1", {"start": v(16.28, 14.6) * mm, "end": v(21.28, 19.6) * mm});
            skLineSegment(sketch, "E12.7.1.2", {"start": v(27.98, 14.6) * mm, "end": v(21.28, 21.3) * mm});
            skLineSegment(sketch, "E12.7.1.3", {"start": v(26.28, 14.6) * mm, "end": v(21.28, 19.6) * mm});
            skLineSegment(sketch, "E12.7.1.4", {"start": v(21.28, 7.9) * mm, "end": v(27.98, 14.6) * mm});
            skLineSegment(sketch, "E12.7.1.5", {"start": v(21.28, 9.6) * mm, "end": v(26.28, 14.6) * mm});
            skLineSegment(sketch, "E12.7.1.6", {"start": v(16.28, 14.6) * mm, "end": v(21.28, 9.6) * mm});
            skLineSegment(sketch, "E12.7.1.7", {"start": v(14.58, 14.6) * mm, "end": v(21.28, 7.9) * mm});
            skLineSegment(sketch, "E12.7.2.0", {"start": v(14.58, 2.8) * mm, "end": v(21.28, 9.5) * mm});
            skLineSegment(sketch, "E12.7.2.1", {"start": v(16.28, 2.8) * mm, "end": v(21.28, 7.8) * mm});
            skLineSegment(sketch, "E12.7.2.2", {"start": v(27.98, 2.8) * mm, "end": v(21.28, 9.5) * mm});
            skLineSegment(sketch, "E12.7.2.3", {"start": v(26.28, 2.8) * mm, "end": v(21.28, 7.8) * mm});
            skLineSegment(sketch, "E12.7.2.4", {"start": v(21.28, -3.9) * mm, "end": v(27.98, 2.8) * mm});
            skLineSegment(sketch, "E12.7.2.5", {"start": v(21.28, -2.2) * mm, "end": v(26.28, 2.8) * mm});
            skLineSegment(sketch, "E12.7.2.6", {"start": v(16.28, 2.8) * mm, "end": v(21.28, -2.2) * mm});
            skLineSegment(sketch, "E12.7.2.7", {"start": v(14.58, 2.8) * mm, "end": v(21.28, -3.9) * mm});
            skLineSegment(sketch, "E12.7.3.0", {"start": v(14.58, -9) * mm, "end": v(21.28, -2.3) * mm});
            skLineSegment(sketch, "E12.7.3.1", {"start": v(16.28, -9) * mm, "end": v(21.28, -4) * mm});
            skLineSegment(sketch, "E12.7.3.2", {"start": v(27.98, -9) * mm, "end": v(21.28, -2.3) * mm});
            skLineSegment(sketch, "E12.7.3.3", {"start": v(26.28, -9) * mm, "end": v(21.28, -4) * mm});
            skLineSegment(sketch, "E12.7.3.4", {"start": v(21.28, -15.7) * mm, "end": v(27.98, -9) * mm});
            skLineSegment(sketch, "E12.7.3.5", {"start": v(21.28, -14) * mm, "end": v(26.28, -9) * mm});
            skLineSegment(sketch, "E12.7.3.6", {"start": v(16.28, -9) * mm, "end": v(21.28, -14) * mm});
            skLineSegment(sketch, "E12.7.3.7", {"start": v(14.58, -9) * mm, "end": v(21.28, -15.7) * mm});
            skLineSegment(sketch, "E12.7.4.0", {"start": v(14.58, -20.8) * mm, "end": v(21.28, -14.1) * mm});
            skLineSegment(sketch, "E12.7.4.1", {"start": v(16.28, -20.8) * mm, "end": v(21.28, -15.8) * mm});
            skLineSegment(sketch, "E12.7.4.2", {"start": v(27.98, -20.8) * mm, "end": v(21.28, -14.1) * mm});
            skLineSegment(sketch, "E12.7.4.3", {"start": v(26.28, -20.8) * mm, "end": v(21.28, -15.8) * mm});
            skLineSegment(sketch, "E12.7.4.4", {"start": v(21.28, -27.5) * mm, "end": v(27.98, -20.8) * mm});
            skLineSegment(sketch, "E12.7.4.5", {"start": v(21.28, -25.8) * mm, "end": v(26.28, -20.8) * mm});
            skLineSegment(sketch, "E12.7.4.6", {"start": v(16.28, -20.8) * mm, "end": v(21.28, -25.8) * mm});
            skLineSegment(sketch, "E12.7.4.7", {"start": v(14.58, -20.8) * mm, "end": v(21.28, -27.5) * mm});
            skLineSegment(sketch, "E12.8.0.0", {"start": v(26.44, 26.4) * mm, "end": v(33.14, 33.1) * mm});
            skLineSegment(sketch, "E12.8.0.1", {"start": v(28.14, 26.4) * mm, "end": v(33.14, 31.4) * mm});
            skLineSegment(sketch, "E12.8.0.2", {"start": v(39.84, 26.4) * mm, "end": v(33.14, 33.1) * mm});
            skLineSegment(sketch, "E12.8.0.3", {"start": v(38.14, 26.4) * mm, "end": v(33.14, 31.4) * mm});
            skLineSegment(sketch, "E12.8.0.4", {"start": v(33.14, 19.7) * mm, "end": v(39.84, 26.4) * mm});
            skLineSegment(sketch, "E12.8.0.5", {"start": v(33.14, 21.4) * mm, "end": v(38.14, 26.4) * mm});
            skLineSegment(sketch, "E12.8.0.6", {"start": v(28.14, 26.4) * mm, "end": v(33.14, 21.4) * mm});
            skLineSegment(sketch, "E12.8.0.7", {"start": v(26.44, 26.4) * mm, "end": v(33.14, 19.7) * mm});
            skLineSegment(sketch, "E12.8.1.0", {"start": v(26.44, 14.6) * mm, "end": v(33.14, 21.3) * mm});
            skLineSegment(sketch, "E12.8.1.1", {"start": v(28.14, 14.6) * mm, "end": v(33.14, 19.6) * mm});
            skLineSegment(sketch, "E12.8.1.2", {"start": v(39.84, 14.6) * mm, "end": v(33.14, 21.3) * mm});
            skLineSegment(sketch, "E12.8.1.3", {"start": v(38.14, 14.6) * mm, "end": v(33.14, 19.6) * mm});
            skLineSegment(sketch, "E12.8.1.4", {"start": v(33.14, 7.9) * mm, "end": v(39.84, 14.6) * mm});
            skLineSegment(sketch, "E12.8.1.5", {"start": v(33.14, 9.6) * mm, "end": v(38.14, 14.6) * mm});
            skLineSegment(sketch, "E12.8.1.6", {"start": v(28.14, 14.6) * mm, "end": v(33.14, 9.6) * mm});
            skLineSegment(sketch, "E12.8.1.7", {"start": v(26.44, 14.6) * mm, "end": v(33.14, 7.9) * mm});
            skLineSegment(sketch, "E12.8.2.0", {"start": v(26.44, 2.8) * mm, "end": v(33.14, 9.5) * mm});
            skLineSegment(sketch, "E12.8.2.1", {"start": v(28.14, 2.8) * mm, "end": v(33.14, 7.8) * mm});
            skLineSegment(sketch, "E12.8.2.2", {"start": v(39.84, 2.8) * mm, "end": v(33.14, 9.5) * mm});
            skLineSegment(sketch, "E12.8.2.3", {"start": v(38.14, 2.8) * mm, "end": v(33.14, 7.8) * mm});
            skLineSegment(sketch, "E12.8.2.4", {"start": v(33.14, -3.9) * mm, "end": v(39.84, 2.8) * mm});
            skLineSegment(sketch, "E12.8.2.5", {"start": v(33.14, -2.2) * mm, "end": v(38.14, 2.8) * mm});
            skLineSegment(sketch, "E12.8.2.6", {"start": v(28.14, 2.8) * mm, "end": v(33.14, -2.2) * mm});
            skLineSegment(sketch, "E12.8.2.7", {"start": v(26.44, 2.8) * mm, "end": v(33.14, -3.9) * mm});
            skLineSegment(sketch, "E12.8.3.0", {"start": v(26.44, -9) * mm, "end": v(33.14, -2.3) * mm});
            skLineSegment(sketch, "E12.8.3.1", {"start": v(28.14, -9) * mm, "end": v(33.14, -4) * mm});
            skLineSegment(sketch, "E12.8.3.2", {"start": v(39.84, -9) * mm, "end": v(33.14, -2.3) * mm});
            skLineSegment(sketch, "E12.8.3.3", {"start": v(38.14, -9) * mm, "end": v(33.14, -4) * mm});
            skLineSegment(sketch, "E12.8.3.4", {"start": v(33.14, -15.7) * mm, "end": v(39.84, -9) * mm});
            skLineSegment(sketch, "E12.8.3.5", {"start": v(33.14, -14) * mm, "end": v(38.14, -9) * mm});
            skLineSegment(sketch, "E12.8.3.6", {"start": v(28.14, -9) * mm, "end": v(33.14, -14) * mm});
            skLineSegment(sketch, "E12.8.3.7", {"start": v(26.44, -9) * mm, "end": v(33.14, -15.7) * mm});
            skLineSegment(sketch, "E12.8.4.0", {"start": v(26.44, -20.8) * mm, "end": v(33.14, -14.1) * mm});
            skLineSegment(sketch, "E12.8.4.1", {"start": v(28.14, -20.8) * mm, "end": v(33.14, -15.8) * mm});
            skLineSegment(sketch, "E12.8.4.2", {"start": v(39.84, -20.8) * mm, "end": v(33.14, -14.1) * mm});
            skLineSegment(sketch, "E12.8.4.3", {"start": v(38.14, -20.8) * mm, "end": v(33.14, -15.8) * mm});
            skLineSegment(sketch, "E12.8.4.4", {"start": v(33.14, -27.5) * mm, "end": v(39.84, -20.8) * mm});
            skLineSegment(sketch, "E12.8.4.5", {"start": v(33.14, -25.8) * mm, "end": v(38.14, -20.8) * mm});
            skLineSegment(sketch, "E12.8.4.6", {"start": v(28.14, -20.8) * mm, "end": v(33.14, -25.8) * mm});
            skLineSegment(sketch, "E12.8.4.7", {"start": v(26.44, -20.8) * mm, "end": v(33.14, -27.5) * mm});
            skLineSegment(sketch, "E12.9.0.0", {"start": v(38.3, 26.4) * mm, "end": v(45, 33.1) * mm});
            skLineSegment(sketch, "E12.9.0.1", {"start": v(40, 26.4) * mm, "end": v(45, 31.4) * mm});
            skLineSegment(sketch, "E12.9.0.2", {"start": v(51.7, 26.4) * mm, "end": v(45, 33.1) * mm});
            skLineSegment(sketch, "E12.9.0.3", {"start": v(50, 26.4) * mm, "end": v(45, 31.4) * mm});
            skLineSegment(sketch, "E12.9.0.4", {"start": v(45, 19.7) * mm, "end": v(51.7, 26.4) * mm});
            skLineSegment(sketch, "E12.9.0.5", {"start": v(45, 21.4) * mm, "end": v(50, 26.4) * mm});
            skLineSegment(sketch, "E12.9.0.6", {"start": v(40, 26.4) * mm, "end": v(45, 21.4) * mm});
            skLineSegment(sketch, "E12.9.0.7", {"start": v(38.3, 26.4) * mm, "end": v(45, 19.7) * mm});
            skLineSegment(sketch, "E12.9.1.0", {"start": v(38.3, 14.6) * mm, "end": v(45, 21.3) * mm});
            skLineSegment(sketch, "E12.9.1.1", {"start": v(40, 14.6) * mm, "end": v(45, 19.6) * mm});
            skLineSegment(sketch, "E12.9.1.2", {"start": v(51.7, 14.6) * mm, "end": v(45, 21.3) * mm});
            skLineSegment(sketch, "E12.9.1.3", {"start": v(50, 14.6) * mm, "end": v(45, 19.6) * mm});
            skLineSegment(sketch, "E12.9.1.4", {"start": v(45, 7.9) * mm, "end": v(51.7, 14.6) * mm});
            skLineSegment(sketch, "E12.9.1.5", {"start": v(45, 9.6) * mm, "end": v(50, 14.6) * mm});
            skLineSegment(sketch, "E12.9.1.6", {"start": v(40, 14.6) * mm, "end": v(45, 9.6) * mm});
            skLineSegment(sketch, "E12.9.1.7", {"start": v(38.3, 14.6) * mm, "end": v(45, 7.9) * mm});
            skLineSegment(sketch, "E12.9.2.0", {"start": v(38.3, 2.8) * mm, "end": v(45, 9.5) * mm});
            skLineSegment(sketch, "E12.9.2.1", {"start": v(40, 2.8) * mm, "end": v(45, 7.8) * mm});
            skLineSegment(sketch, "E12.9.2.2", {"start": v(51.7, 2.8) * mm, "end": v(45, 9.5) * mm});
            skLineSegment(sketch, "E12.9.2.3", {"start": v(50, 2.8) * mm, "end": v(45, 7.8) * mm});
            skLineSegment(sketch, "E12.9.2.4", {"start": v(45, -3.9) * mm, "end": v(51.7, 2.8) * mm});
            skLineSegment(sketch, "E12.9.2.5", {"start": v(45, -2.2) * mm, "end": v(50, 2.8) * mm});
            skLineSegment(sketch, "E12.9.2.6", {"start": v(40, 2.8) * mm, "end": v(45, -2.2) * mm});
            skLineSegment(sketch, "E12.9.2.7", {"start": v(38.3, 2.8) * mm, "end": v(45, -3.9) * mm});
            skLineSegment(sketch, "E12.9.3.0", {"start": v(38.3, -9) * mm, "end": v(45, -2.3) * mm});
            skLineSegment(sketch, "E12.9.3.1", {"start": v(40, -9) * mm, "end": v(45, -4) * mm});
            skLineSegment(sketch, "E12.9.3.2", {"start": v(51.7, -9) * mm, "end": v(45, -2.3) * mm});
            skLineSegment(sketch, "E12.9.3.3", {"start": v(50, -9) * mm, "end": v(45, -4) * mm});
            skLineSegment(sketch, "E12.9.3.4", {"start": v(45, -15.7) * mm, "end": v(51.7, -9) * mm});
            skLineSegment(sketch, "E12.9.3.5", {"start": v(45, -14) * mm, "end": v(50, -9) * mm});
            skLineSegment(sketch, "E12.9.3.6", {"start": v(40, -9) * mm, "end": v(45, -14) * mm});
            skLineSegment(sketch, "E12.9.3.7", {"start": v(38.3, -9) * mm, "end": v(45, -15.7) * mm});
            skLineSegment(sketch, "E12.9.4.0", {"start": v(38.3, -20.8) * mm, "end": v(45, -14.1) * mm});
            skLineSegment(sketch, "E12.9.4.1", {"start": v(40, -20.8) * mm, "end": v(45, -15.8) * mm});
            skLineSegment(sketch, "E12.9.4.2", {"start": v(51.7, -20.8) * mm, "end": v(45, -14.1) * mm});
            skLineSegment(sketch, "E12.9.4.3", {"start": v(50, -20.8) * mm, "end": v(45, -15.8) * mm});
            skLineSegment(sketch, "E12.9.4.4", {"start": v(45, -27.5) * mm, "end": v(51.7, -20.8) * mm});
            skLineSegment(sketch, "E12.9.4.5", {"start": v(45, -25.8) * mm, "end": v(50, -20.8) * mm});
            skLineSegment(sketch, "E12.9.4.6", {"start": v(40, -20.8) * mm, "end": v(45, -25.8) * mm});
            skLineSegment(sketch, "E12.9.4.7", {"start": v(38.3, -20.8) * mm, "end": v(45, -27.5) * mm});
            skLineSegment(sketch, "E12.10.0.0", {"start": v(50.16, 26.4) * mm, "end": v(56.86, 33.1) * mm});
            skLineSegment(sketch, "E12.10.0.1", {"start": v(51.86, 26.4) * mm, "end": v(56.86, 31.4) * mm});
            skLineSegment(sketch, "E12.10.0.2", {"start": v(63.56, 26.4) * mm, "end": v(56.86, 33.1) * mm});
            skLineSegment(sketch, "E12.10.0.3", {"start": v(61.86, 26.4) * mm, "end": v(56.86, 31.4) * mm});
            skLineSegment(sketch, "E12.10.0.4", {"start": v(56.86, 19.7) * mm, "end": v(63.56, 26.4) * mm});
            skLineSegment(sketch, "E12.10.0.5", {"start": v(56.86, 21.4) * mm, "end": v(61.86, 26.4) * mm});
            skLineSegment(sketch, "E12.10.0.6", {"start": v(51.86, 26.4) * mm, "end": v(56.86, 21.4) * mm});
            skLineSegment(sketch, "E12.10.0.7", {"start": v(50.16, 26.4) * mm, "end": v(56.86, 19.7) * mm});
            skLineSegment(sketch, "E12.10.1.0", {"start": v(50.16, 14.6) * mm, "end": v(56.86, 21.3) * mm});
            skLineSegment(sketch, "E12.10.1.1", {"start": v(51.86, 14.6) * mm, "end": v(56.86, 19.6) * mm});
            skLineSegment(sketch, "E12.10.1.2", {"start": v(63.56, 14.6) * mm, "end": v(56.86, 21.3) * mm});
            skLineSegment(sketch, "E12.10.1.3", {"start": v(61.86, 14.6) * mm, "end": v(56.86, 19.6) * mm});
            skLineSegment(sketch, "E12.10.1.4", {"start": v(56.86, 7.9) * mm, "end": v(63.56, 14.6) * mm});
            skLineSegment(sketch, "E12.10.1.5", {"start": v(56.86, 9.6) * mm, "end": v(61.86, 14.6) * mm});
            skLineSegment(sketch, "E12.10.1.6", {"start": v(51.86, 14.6) * mm, "end": v(56.86, 9.6) * mm});
            skLineSegment(sketch, "E12.10.1.7", {"start": v(50.16, 14.6) * mm, "end": v(56.86, 7.9) * mm});
            skLineSegment(sketch, "E12.10.2.0", {"start": v(50.16, 2.8) * mm, "end": v(56.86, 9.5) * mm});
            skLineSegment(sketch, "E12.10.2.1", {"start": v(51.86, 2.8) * mm, "end": v(56.86, 7.8) * mm});
            skLineSegment(sketch, "E12.10.2.2", {"start": v(63.56, 2.8) * mm, "end": v(56.86, 9.5) * mm});
            skLineSegment(sketch, "E12.10.2.3", {"start": v(61.86, 2.8) * mm, "end": v(56.86, 7.8) * mm});
            skLineSegment(sketch, "E12.10.2.4", {"start": v(56.86, -3.9) * mm, "end": v(63.56, 2.8) * mm});
            skLineSegment(sketch, "E12.10.2.5", {"start": v(56.86, -2.2) * mm, "end": v(61.86, 2.8) * mm});
            skLineSegment(sketch, "E12.10.2.6", {"start": v(51.86, 2.8) * mm, "end": v(56.86, -2.2) * mm});
            skLineSegment(sketch, "E12.10.2.7", {"start": v(50.16, 2.8) * mm, "end": v(56.86, -3.9) * mm});
            skLineSegment(sketch, "E12.10.3.0", {"start": v(50.16, -9) * mm, "end": v(56.86, -2.3) * mm});
            skLineSegment(sketch, "E12.10.3.1", {"start": v(51.86, -9) * mm, "end": v(56.86, -4) * mm});
            skLineSegment(sketch, "E12.10.3.2", {"start": v(63.56, -9) * mm, "end": v(56.86, -2.3) * mm});
            skLineSegment(sketch, "E12.10.3.3", {"start": v(61.86, -9) * mm, "end": v(56.86, -4) * mm});
            skLineSegment(sketch, "E12.10.3.4", {"start": v(56.86, -15.7) * mm, "end": v(63.56, -9) * mm});
            skLineSegment(sketch, "E12.10.3.5", {"start": v(56.86, -14) * mm, "end": v(61.86, -9) * mm});
            skLineSegment(sketch, "E12.10.3.6", {"start": v(51.86, -9) * mm, "end": v(56.86, -14) * mm});
            skLineSegment(sketch, "E12.10.3.7", {"start": v(50.16, -9) * mm, "end": v(56.86, -15.7) * mm});
            skLineSegment(sketch, "E12.10.4.0", {"start": v(50.16, -20.8) * mm, "end": v(56.86, -14.1) * mm});
            skLineSegment(sketch, "E12.10.4.1", {"start": v(51.86, -20.8) * mm, "end": v(56.86, -15.8) * mm});
            skLineSegment(sketch, "E12.10.4.2", {"start": v(63.56, -20.8) * mm, "end": v(56.86, -14.1) * mm});
            skLineSegment(sketch, "E12.10.4.3", {"start": v(61.86, -20.8) * mm, "end": v(56.86, -15.8) * mm});
            skLineSegment(sketch, "E12.10.4.4", {"start": v(56.86, -27.5) * mm, "end": v(63.56, -20.8) * mm});
            skLineSegment(sketch, "E12.10.4.5", {"start": v(56.86, -25.8) * mm, "end": v(61.86, -20.8) * mm});
            skLineSegment(sketch, "E12.10.4.6", {"start": v(51.86, -20.8) * mm, "end": v(56.86, -25.8) * mm});
            skLineSegment(sketch, "E12.10.4.7", {"start": v(50.16, -20.8) * mm, "end": v(56.86, -27.5) * mm});
            skLineSegment(sketch, "E12.11.0.0", {"start": v(62.02, 26.4) * mm, "end": v(68.72, 33.1) * mm});
            skLineSegment(sketch, "E12.11.0.1", {"start": v(63.72, 26.4) * mm, "end": v(68.72, 31.4) * mm});
            skLineSegment(sketch, "E12.11.0.2", {"start": v(75.42, 26.4) * mm, "end": v(68.72, 33.1) * mm});
            skLineSegment(sketch, "E12.11.0.3", {"start": v(73.72, 26.4) * mm, "end": v(68.72, 31.4) * mm});
            skLineSegment(sketch, "E12.11.0.4", {"start": v(68.72, 19.7) * mm, "end": v(75.42, 26.4) * mm});
            skLineSegment(sketch, "E12.11.0.5", {"start": v(68.72, 21.4) * mm, "end": v(73.72, 26.4) * mm});
            skLineSegment(sketch, "E12.11.0.6", {"start": v(63.72, 26.4) * mm, "end": v(68.72, 21.4) * mm});
            skLineSegment(sketch, "E12.11.0.7", {"start": v(62.02, 26.4) * mm, "end": v(68.72, 19.7) * mm});
            skLineSegment(sketch, "E12.11.1.0", {"start": v(62.02, 14.6) * mm, "end": v(68.72, 21.3) * mm});
            skLineSegment(sketch, "E12.11.1.1", {"start": v(63.72, 14.6) * mm, "end": v(68.72, 19.6) * mm});
            skLineSegment(sketch, "E12.11.1.2", {"start": v(75.42, 14.6) * mm, "end": v(68.72, 21.3) * mm});
            skLineSegment(sketch, "E12.11.1.3", {"start": v(73.72, 14.6) * mm, "end": v(68.72, 19.6) * mm});
            skLineSegment(sketch, "E12.11.1.4", {"start": v(68.72, 7.9) * mm, "end": v(75.42, 14.6) * mm});
            skLineSegment(sketch, "E12.11.1.5", {"start": v(68.72, 9.6) * mm, "end": v(73.72, 14.6) * mm});
            skLineSegment(sketch, "E12.11.1.6", {"start": v(63.72, 14.6) * mm, "end": v(68.72, 9.6) * mm});
            skLineSegment(sketch, "E12.11.1.7", {"start": v(62.02, 14.6) * mm, "end": v(68.72, 7.9) * mm});
            skLineSegment(sketch, "E12.11.2.0", {"start": v(62.02, 2.8) * mm, "end": v(68.72, 9.5) * mm});
            skLineSegment(sketch, "E12.11.2.1", {"start": v(63.72, 2.8) * mm, "end": v(68.72, 7.8) * mm});
            skLineSegment(sketch, "E12.11.2.2", {"start": v(75.42, 2.8) * mm, "end": v(68.72, 9.5) * mm});
            skLineSegment(sketch, "E12.11.2.3", {"start": v(73.72, 2.8) * mm, "end": v(68.72, 7.8) * mm});
            skLineSegment(sketch, "E12.11.2.4", {"start": v(68.72, -3.9) * mm, "end": v(75.42, 2.8) * mm});
            skLineSegment(sketch, "E12.11.2.5", {"start": v(68.72, -2.2) * mm, "end": v(73.72, 2.8) * mm});
            skLineSegment(sketch, "E12.11.2.6", {"start": v(63.72, 2.8) * mm, "end": v(68.72, -2.2) * mm});
            skLineSegment(sketch, "E12.11.2.7", {"start": v(62.02, 2.8) * mm, "end": v(68.72, -3.9) * mm});
            skLineSegment(sketch, "E12.11.3.0", {"start": v(62.02, -9) * mm, "end": v(68.72, -2.3) * mm});
            skLineSegment(sketch, "E12.11.3.1", {"start": v(63.72, -9) * mm, "end": v(68.72, -4) * mm});
            skLineSegment(sketch, "E12.11.3.2", {"start": v(75.42, -9) * mm, "end": v(68.72, -2.3) * mm});
            skLineSegment(sketch, "E12.11.3.3", {"start": v(73.72, -9) * mm, "end": v(68.72, -4) * mm});
            skLineSegment(sketch, "E12.11.3.4", {"start": v(68.72, -15.7) * mm, "end": v(75.42, -9) * mm});
            skLineSegment(sketch, "E12.11.3.5", {"start": v(68.72, -14) * mm, "end": v(73.72, -9) * mm});
            skLineSegment(sketch, "E12.11.3.6", {"start": v(63.72, -9) * mm, "end": v(68.72, -14) * mm});
            skLineSegment(sketch, "E12.11.3.7", {"start": v(62.02, -9) * mm, "end": v(68.72, -15.7) * mm});
            skLineSegment(sketch, "E12.11.4.0", {"start": v(62.02, -20.8) * mm, "end": v(68.72, -14.1) * mm});
            skLineSegment(sketch, "E12.11.4.1", {"start": v(63.72, -20.8) * mm, "end": v(68.72, -15.8) * mm});
            skLineSegment(sketch, "E12.11.4.2", {"start": v(75.42, -20.8) * mm, "end": v(68.72, -14.1) * mm});
            skLineSegment(sketch, "E12.11.4.3", {"start": v(73.72, -20.8) * mm, "end": v(68.72, -15.8) * mm});
            skLineSegment(sketch, "E12.11.4.4", {"start": v(68.72, -27.5) * mm, "end": v(75.42, -20.8) * mm});
            skLineSegment(sketch, "E12.11.4.5", {"start": v(68.72, -25.8) * mm, "end": v(73.72, -20.8) * mm});
            skLineSegment(sketch, "E12.11.4.6", {"start": v(63.72, -20.8) * mm, "end": v(68.72, -25.8) * mm});
            skLineSegment(sketch, "E12.11.4.7", {"start": v(62.02, -20.8) * mm, "end": v(68.72, -27.5) * mm});
            skLineSegment(sketch, "E12.direction1", {"start": v(-68.44, 26.4) * mm, "end": v(-56.58, 26.4) * mm, "construction": true});
            skLineSegment(sketch, "E12.direction2", {"start": v(-68.44, 26.4) * mm, "end": v(-68.44, 14.6) * mm, "construction": true});
            skSolve(sketch);
        }
        {
            var Q0;
            {var subQ5=makeQuery(id+"F4.opExtrude","CAP_EDGE",EDGE,{"disambiguationData":[OSD([sQuery(id+"F3.wireOp",EDGE,"E6.0")])],"isStart":true});Q0=makeQuery(id+"F5.imprint","IMPRINT",FACE,{"disambiguationData":[TD([[makeQuery(id+"F5.imprint","IMPRINT",EDGE,{"derivedFrom":subQ5}),1.0]])]});}
            var Q1;
            Q1=makeQuery(id+"F5.imprint","IMPRINT",FACE,{"disambiguationData":[TD([[makeQuery(id+"F5.imprint","IMPRINT",EDGE,{"derivedFrom":sQuery(id+"F5.wireOp",EDGE,"E7")}),-1.0]])]});
            var Q2;
            {var subQ0=sQuery(id+"F5.wireOp",EDGE,"E12.0.1.0");var subQ1=sQuery(id+"F5.wireOp",EDGE,"E11.1");var subQ2=makeQuery(id+"F5.imprint","INTERSECT",VERTEX,{"derivedFrom":[subQ1,subQ0]});Q2=makeQuery(id+"F5.imprint","IMPRINT",FACE,{"disambiguationData":[TD([[makeQuery(id+"F5.imprint","IMPRINT",EDGE,{"disambiguationData":[TD([[subQ2,1.0]])],"derivedFrom":subQ1}),-1.0]])]});}
            var Q3;
            Q3=makeQuery(id+"F5.imprint","IMPRINT",FACE,{"disambiguationData":[TD([[makeQuery(id+"F5.imprint","IMPRINT",EDGE,{"derivedFrom":sQuery(id+"F5.wireOp",EDGE,"E12.0.1.1")}),-1.0]])]});
            var Q4;
            {var subQ0=sQuery(id+"F5.wireOp",EDGE,"E12.0.1.2");var subQ1=sQuery(id+"F5.wireOp",EDGE,"E11.0");var subQ2=makeQuery(id+"F5.imprint","INTERSECT",VERTEX,{"derivedFrom":[subQ1,subQ0]});Q4=makeQuery(id+"F5.imprint","IMPRINT",FACE,{"disambiguationData":[TD([[makeQuery(id+"F5.imprint","IMPRINT",EDGE,{"disambiguationData":[TD([[subQ2,-1.0]])],"derivedFrom":subQ1}),-1.0]])]});}
            var Q5;
            {var subQ0=sQuery(id+"F5.wireOp",EDGE,"E12.1.0.0");var subQ1=sQuery(id+"F5.wireOp",EDGE,"E11.3");var subQ2=makeQuery(id+"F5.imprint","INTERSECT",VERTEX,{"derivedFrom":[subQ1,subQ0]});Q5=makeQuery(id+"F5.imprint","IMPRINT",FACE,{"disambiguationData":[TD([[makeQuery(id+"F5.imprint","IMPRINT",EDGE,{"disambiguationData":[TD([[subQ2,-1.0]])],"derivedFrom":subQ1}),-1.0]])]});}
            var Q6;
            {var subQ0=sQuery(id+"F5.wireOp",EDGE,"E12.2.0.0");var subQ1=sQuery(id+"F5.wireOp",EDGE,"E12.1.0.2");var subQ2=makeQuery(id+"F5.imprint","INTERSECT",VERTEX,{"derivedFrom":[subQ1,subQ0]});Q6=makeQuery(id+"F5.imprint","IMPRINT",FACE,{"disambiguationData":[TD([[makeQuery(id+"F5.imprint","IMPRINT",EDGE,{"disambiguationData":[TD([[subQ2,-1.0]])],"derivedFrom":subQ1}),-1.0]])]});}
            var Q7;
            {var subQ0=sQuery(id+"F5.wireOp",EDGE,"E12.3.0.0");var subQ1=sQuery(id+"F5.wireOp",EDGE,"E12.2.0.2");var subQ2=makeQuery(id+"F5.imprint","INTERSECT",VERTEX,{"derivedFrom":[subQ1,subQ0]});Q7=makeQuery(id+"F5.imprint","IMPRINT",FACE,{"disambiguationData":[TD([[makeQuery(id+"F5.imprint","IMPRINT",EDGE,{"disambiguationData":[TD([[subQ2,-1.0]])],"derivedFrom":subQ1}),-1.0]])]});}
            var Q8;
            {var subQ0=sQuery(id+"F5.wireOp",EDGE,"E12.0.2.0");var subQ1=sQuery(id+"F5.wireOp",EDGE,"E12.0.1.7");var subQ2=makeQuery(id+"F5.imprint","INTERSECT",VERTEX,{"derivedFrom":[subQ1,subQ0]});Q8=makeQuery(id+"F5.imprint","IMPRINT",FACE,{"disambiguationData":[TD([[makeQuery(id+"F5.imprint","IMPRINT",EDGE,{"disambiguationData":[TD([[subQ2,1.0]])],"derivedFrom":subQ1}),-1.0]])]});}
            var Q9;
            Q9=makeQuery(id+"F5.imprint","IMPRINT",FACE,{"disambiguationData":[TD([[makeQuery(id+"F5.imprint","IMPRINT",EDGE,{"derivedFrom":sQuery(id+"F5.wireOp",EDGE,"E12.0.2.1")}),-1.0]])]});
            var Q10;
            {var subQ0=sQuery(id+"F5.wireOp",EDGE,"E12.0.3.0");var subQ1=sQuery(id+"F5.wireOp",EDGE,"E12.0.2.7");var subQ2=makeQuery(id+"F5.imprint","INTERSECT",VERTEX,{"derivedFrom":[subQ1,subQ0]});Q10=makeQuery(id+"F5.imprint","IMPRINT",FACE,{"disambiguationData":[TD([[makeQuery(id+"F5.imprint","IMPRINT",EDGE,{"disambiguationData":[TD([[subQ2,1.0]])],"derivedFrom":subQ1}),-1.0]])]});}
            var Q11;
            Q11=makeQuery(id+"F5.imprint","IMPRINT",FACE,{"disambiguationData":[TD([[makeQuery(id+"F5.imprint","IMPRINT",EDGE,{"derivedFrom":sQuery(id+"F5.wireOp",EDGE,"E12.0.3.1")}),-1.0]])]});
            var Q12;
            {var subQ0=sQuery(id+"F5.wireOp",EDGE,"E12.0.3.2");var subQ1=sQuery(id+"F5.wireOp",EDGE,"E12.0.2.4");var subQ2=makeQuery(id+"F5.imprint","INTERSECT",VERTEX,{"derivedFrom":[subQ1,subQ0]});Q12=makeQuery(id+"F5.imprint","IMPRINT",FACE,{"disambiguationData":[TD([[makeQuery(id+"F5.imprint","IMPRINT",EDGE,{"disambiguationData":[TD([[subQ2,-1.0]])],"derivedFrom":subQ1}),-1.0]])]});}
            var Q13;
            {var subQ0=sQuery(id+"F5.wireOp",EDGE,"E12.0.4.0");var subQ1=sQuery(id+"F5.wireOp",EDGE,"E12.0.3.7");var subQ2=makeQuery(id+"F5.imprint","INTERSECT",VERTEX,{"derivedFrom":[subQ1,subQ0]});Q13=makeQuery(id+"F5.imprint","IMPRINT",FACE,{"disambiguationData":[TD([[makeQuery(id+"F5.imprint","IMPRINT",EDGE,{"disambiguationData":[TD([[subQ2,1.0]])],"derivedFrom":subQ1}),-1.0]])]});}
            var Q14;
            {var subQ6=sQuery(id+"F5.wireOp",EDGE,"E12.0.4.1");Q14=makeQuery(id+"F5.imprint","IMPRINT",FACE,{"disambiguationData":[TD([[makeQuery(id+"F5.imprint","IMPRINT",EDGE,{"derivedFrom":subQ6}),-1.0]])]});}
            var Q15;
            {var subQ5=sQuery(id+"F5.wireOp",EDGE,"E12.1.4.1");Q15=makeQuery(id+"F5.imprint","IMPRINT",FACE,{"disambiguationData":[TD([[makeQuery(id+"F5.imprint","IMPRINT",EDGE,{"derivedFrom":subQ5}),-1.0]])]});}
            var Q16;
            {var subQ5=sQuery(id+"F5.wireOp",EDGE,"E12.2.4.1");Q16=makeQuery(id+"F5.imprint","IMPRINT",FACE,{"disambiguationData":[TD([[makeQuery(id+"F5.imprint","IMPRINT",EDGE,{"derivedFrom":subQ5}),-1.0]])]});}
            var Q17;
            {var subQ5=sQuery(id+"F5.wireOp",EDGE,"E12.3.4.1");Q17=makeQuery(id+"F5.imprint","IMPRINT",FACE,{"disambiguationData":[TD([[makeQuery(id+"F5.imprint","IMPRINT",EDGE,{"derivedFrom":subQ5}),-1.0]])]});}
            var Q18;
            {var subQ5=sQuery(id+"F5.wireOp",EDGE,"E12.4.4.1");Q18=makeQuery(id+"F5.imprint","IMPRINT",FACE,{"disambiguationData":[TD([[makeQuery(id+"F5.imprint","IMPRINT",EDGE,{"derivedFrom":subQ5}),-1.0]])]});}
            var Q19;
            {var subQ5=sQuery(id+"F5.wireOp",EDGE,"E12.5.4.1");Q19=makeQuery(id+"F5.imprint","IMPRINT",FACE,{"disambiguationData":[TD([[makeQuery(id+"F5.imprint","IMPRINT",EDGE,{"derivedFrom":subQ5}),-1.0]])]});}
            var Q20;
            {var subQ6=sQuery(id+"F5.wireOp",EDGE,"E12.6.4.1");Q20=makeQuery(id+"F5.imprint","IMPRINT",FACE,{"disambiguationData":[TD([[makeQuery(id+"F5.imprint","IMPRINT",EDGE,{"derivedFrom":subQ6}),-1.0]])]});}
            var Q21;
            {var subQ5=sQuery(id+"F5.wireOp",EDGE,"E12.7.4.1");Q21=makeQuery(id+"F5.imprint","IMPRINT",FACE,{"disambiguationData":[TD([[makeQuery(id+"F5.imprint","IMPRINT",EDGE,{"derivedFrom":subQ5}),-1.0]])]});}
            var Q22;
            {var subQ5=sQuery(id+"F5.wireOp",EDGE,"E12.8.4.1");Q22=makeQuery(id+"F5.imprint","IMPRINT",FACE,{"disambiguationData":[TD([[makeQuery(id+"F5.imprint","IMPRINT",EDGE,{"derivedFrom":subQ5}),-1.0]])]});}
            var Q23;
            {var subQ5=sQuery(id+"F5.wireOp",EDGE,"E12.9.4.1");Q23=makeQuery(id+"F5.imprint","IMPRINT",FACE,{"disambiguationData":[TD([[makeQuery(id+"F5.imprint","IMPRINT",EDGE,{"derivedFrom":subQ5}),-1.0]])]});}
            var Q24;
            {var subQ6=sQuery(id+"F5.wireOp",EDGE,"E12.10.4.1");Q24=makeQuery(id+"F5.imprint","IMPRINT",FACE,{"disambiguationData":[TD([[makeQuery(id+"F5.imprint","IMPRINT",EDGE,{"derivedFrom":subQ6}),-1.0]])]});}
            var Q25;
            {var subQ1=sQuery(id+"F5.wireOp",EDGE,"E12.10.4.2");var subQ6=sQuery(id+"F5.wireOp",EDGE,"E12.10.3.4");var subQ9=makeQuery(id+"F5.imprint","INTERSECT",VERTEX,{"derivedFrom":[subQ6,subQ1]});Q25=makeQuery(id+"F5.imprint","IMPRINT",FACE,{"disambiguationData":[TD([[makeQuery(id+"F5.imprint","IMPRINT",EDGE,{"disambiguationData":[TD([[subQ9,-1.0]])],"derivedFrom":subQ6}),-1.0]])]});}
            var Q26;
            {var subQ1=sQuery(id+"F5.wireOp",EDGE,"E12.10.3.2");var subQ5=sQuery(id+"F5.wireOp",EDGE,"E12.10.2.4");var subQ6=makeQuery(id+"F5.imprint","INTERSECT",VERTEX,{"derivedFrom":[subQ5,subQ1]});Q26=makeQuery(id+"F5.imprint","IMPRINT",FACE,{"disambiguationData":[TD([[makeQuery(id+"F5.imprint","IMPRINT",EDGE,{"disambiguationData":[TD([[subQ6,-1.0]])],"derivedFrom":subQ5}),-1.0]])]});}
            var Q27;
            {var subQ1=sQuery(id+"F5.wireOp",EDGE,"E12.10.1.4");var subQ5=sQuery(id+"F5.wireOp",EDGE,"E12.10.2.2");var subQ6=makeQuery(id+"F5.imprint","INTERSECT",VERTEX,{"derivedFrom":[subQ1,subQ5]});Q27=makeQuery(id+"F5.imprint","IMPRINT",FACE,{"disambiguationData":[TD([[makeQuery(id+"F5.imprint","IMPRINT",EDGE,{"disambiguationData":[TD([[subQ6,-1.0]])],"derivedFrom":subQ1}),-1.0]])]});}
            var Q28;
            {var subQ1=sQuery(id+"F5.wireOp",EDGE,"E12.10.0.4");var subQ5=sQuery(id+"F5.wireOp",EDGE,"E12.10.1.2");var subQ6=makeQuery(id+"F5.imprint","INTERSECT",VERTEX,{"derivedFrom":[subQ1,subQ5]});Q28=makeQuery(id+"F5.imprint","IMPRINT",FACE,{"disambiguationData":[TD([[makeQuery(id+"F5.imprint","IMPRINT",EDGE,{"disambiguationData":[TD([[subQ6,-1.0]])],"derivedFrom":subQ1}),-1.0]])]});}
            var Q29;
            {var subQ0=sQuery(id+"F5.wireOp",EDGE,"E12.11.0.0");var subQ1=sQuery(id+"F5.wireOp",EDGE,"E12.10.0.2");var subQ2=makeQuery(id+"F5.imprint","INTERSECT",VERTEX,{"derivedFrom":[subQ1,subQ0]});Q29=makeQuery(id+"F5.imprint","IMPRINT",FACE,{"disambiguationData":[TD([[makeQuery(id+"F5.imprint","IMPRINT",EDGE,{"disambiguationData":[TD([[subQ2,-1.0]])],"derivedFrom":subQ1}),-1.0]])]});}
            var Q30;
            Q30=makeQuery(id+"F5.imprint","IMPRINT",FACE,{"disambiguationData":[TD([[makeQuery(id+"F5.imprint","IMPRINT",EDGE,{"derivedFrom":sQuery(id+"F5.wireOp",EDGE,"E12.10.0.1")}),-1.0]])]});
            var Q31;
            Q31=makeQuery(id+"F5.imprint","IMPRINT",FACE,{"disambiguationData":[TD([[makeQuery(id+"F5.imprint","IMPRINT",EDGE,{"derivedFrom":sQuery(id+"F5.wireOp",EDGE,"E12.9.0.1")}),-1.0]])]});
            var Q32;
            Q32=makeQuery(id+"F5.imprint","IMPRINT",FACE,{"disambiguationData":[TD([[makeQuery(id+"F5.imprint","IMPRINT",EDGE,{"derivedFrom":sQuery(id+"F5.wireOp",EDGE,"E12.8.0.1")}),-1.0]])]});
            var Q33;
            Q33=makeQuery(id+"F5.imprint","IMPRINT",FACE,{"disambiguationData":[TD([[makeQuery(id+"F5.imprint","IMPRINT",EDGE,{"derivedFrom":sQuery(id+"F5.wireOp",EDGE,"E12.7.0.1")}),-1.0]])]});
            var Q34;
            Q34=makeQuery(id+"F5.imprint","IMPRINT",FACE,{"disambiguationData":[TD([[makeQuery(id+"F5.imprint","IMPRINT",EDGE,{"derivedFrom":sQuery(id+"F5.wireOp",EDGE,"E12.6.0.1")}),-1.0]])]});
            var Q35;
            Q35=makeQuery(id+"F5.imprint","IMPRINT",FACE,{"disambiguationData":[TD([[makeQuery(id+"F5.imprint","IMPRINT",EDGE,{"derivedFrom":sQuery(id+"F5.wireOp",EDGE,"E12.5.0.1")}),-1.0]])]});
            var Q36;
            Q36=makeQuery(id+"F5.imprint","IMPRINT",FACE,{"disambiguationData":[TD([[makeQuery(id+"F5.imprint","IMPRINT",EDGE,{"derivedFrom":sQuery(id+"F5.wireOp",EDGE,"E12.4.0.1")}),-1.0]])]});
            var Q37;
            Q37=makeQuery(id+"F5.imprint","IMPRINT",FACE,{"disambiguationData":[TD([[makeQuery(id+"F5.imprint","IMPRINT",EDGE,{"derivedFrom":sQuery(id+"F5.wireOp",EDGE,"E12.3.0.1")}),-1.0]])]});
            var Q38;
            Q38=makeQuery(id+"F5.imprint","IMPRINT",FACE,{"disambiguationData":[TD([[makeQuery(id+"F5.imprint","IMPRINT",EDGE,{"derivedFrom":sQuery(id+"F5.wireOp",EDGE,"E12.2.0.1")}),-1.0]])]});
            var Q39;
            {var subQ0=sQuery(id+"F5.wireOp",EDGE,"E12.4.0.0");var subQ1=sQuery(id+"F5.wireOp",EDGE,"E12.3.0.2");var subQ2=makeQuery(id+"F5.imprint","INTERSECT",VERTEX,{"derivedFrom":[subQ1,subQ0]});Q39=makeQuery(id+"F5.imprint","IMPRINT",FACE,{"disambiguationData":[TD([[makeQuery(id+"F5.imprint","IMPRINT",EDGE,{"disambiguationData":[TD([[subQ2,-1.0]])],"derivedFrom":subQ1}),-1.0]])]});}
            var Q40;
            {var subQ0=sQuery(id+"F5.wireOp",EDGE,"E12.5.0.0");var subQ1=sQuery(id+"F5.wireOp",EDGE,"E12.4.0.2");var subQ2=makeQuery(id+"F5.imprint","INTERSECT",VERTEX,{"derivedFrom":[subQ1,subQ0]});Q40=makeQuery(id+"F5.imprint","IMPRINT",FACE,{"disambiguationData":[TD([[makeQuery(id+"F5.imprint","IMPRINT",EDGE,{"disambiguationData":[TD([[subQ2,-1.0]])],"derivedFrom":subQ1}),-1.0]])]});}
            var Q41;
            {var subQ0=sQuery(id+"F5.wireOp",EDGE,"E12.6.0.0");var subQ1=sQuery(id+"F5.wireOp",EDGE,"E12.5.0.2");var subQ2=makeQuery(id+"F5.imprint","INTERSECT",VERTEX,{"derivedFrom":[subQ1,subQ0]});Q41=makeQuery(id+"F5.imprint","IMPRINT",FACE,{"disambiguationData":[TD([[makeQuery(id+"F5.imprint","IMPRINT",EDGE,{"disambiguationData":[TD([[subQ2,-1.0]])],"derivedFrom":subQ1}),-1.0]])]});}
            var Q42;
            {var subQ0=sQuery(id+"F5.wireOp",EDGE,"E12.7.0.0");var subQ1=sQuery(id+"F5.wireOp",EDGE,"E12.6.0.2");var subQ2=makeQuery(id+"F5.imprint","INTERSECT",VERTEX,{"derivedFrom":[subQ1,subQ0]});Q42=makeQuery(id+"F5.imprint","IMPRINT",FACE,{"disambiguationData":[TD([[makeQuery(id+"F5.imprint","IMPRINT",EDGE,{"disambiguationData":[TD([[subQ2,-1.0]])],"derivedFrom":subQ1}),-1.0]])]});}
            var Q43;
            {var subQ0=sQuery(id+"F5.wireOp",EDGE,"E12.8.0.0");var subQ1=sQuery(id+"F5.wireOp",EDGE,"E12.7.0.2");var subQ2=makeQuery(id+"F5.imprint","INTERSECT",VERTEX,{"derivedFrom":[subQ1,subQ0]});Q43=makeQuery(id+"F5.imprint","IMPRINT",FACE,{"disambiguationData":[TD([[makeQuery(id+"F5.imprint","IMPRINT",EDGE,{"disambiguationData":[TD([[subQ2,-1.0]])],"derivedFrom":subQ1}),-1.0]])]});}
            var Q44;
            {var subQ0=sQuery(id+"F5.wireOp",EDGE,"E12.9.0.0");var subQ1=sQuery(id+"F5.wireOp",EDGE,"E12.8.0.2");var subQ2=makeQuery(id+"F5.imprint","INTERSECT",VERTEX,{"derivedFrom":[subQ1,subQ0]});Q44=makeQuery(id+"F5.imprint","IMPRINT",FACE,{"disambiguationData":[TD([[makeQuery(id+"F5.imprint","IMPRINT",EDGE,{"disambiguationData":[TD([[subQ2,-1.0]])],"derivedFrom":subQ1}),-1.0]])]});}
            var Q45;
            {var subQ0=sQuery(id+"F5.wireOp",EDGE,"E12.10.0.0");var subQ1=sQuery(id+"F5.wireOp",EDGE,"E12.9.0.2");var subQ2=makeQuery(id+"F5.imprint","INTERSECT",VERTEX,{"derivedFrom":[subQ1,subQ0]});Q45=makeQuery(id+"F5.imprint","IMPRINT",FACE,{"disambiguationData":[TD([[makeQuery(id+"F5.imprint","IMPRINT",EDGE,{"disambiguationData":[TD([[subQ2,-1.0]])],"derivedFrom":subQ1}),-1.0]])]});}
            var Q46;
            Q46=makeQuery(id+"F5.imprint","IMPRINT",FACE,{"disambiguationData":[TD([[makeQuery(id+"F5.imprint","IMPRINT",EDGE,{"derivedFrom":sQuery(id+"F5.wireOp",EDGE,"E12.1.0.1")}),-1.0]])]});
            var Q47;
            {var subQ0=sQuery(id+"F5.wireOp",EDGE,"E12.1.1.2");var subQ1=sQuery(id+"F5.wireOp",EDGE,"E12.1.0.4");var subQ2=makeQuery(id+"F5.imprint","INTERSECT",VERTEX,{"derivedFrom":[subQ1,subQ0]});Q47=makeQuery(id+"F5.imprint","IMPRINT",FACE,{"disambiguationData":[TD([[makeQuery(id+"F5.imprint","IMPRINT",EDGE,{"disambiguationData":[TD([[subQ2,-1.0]])],"derivedFrom":subQ1}),-1.0]])]});}
            var Q48;
            Q48=makeQuery(id+"F5.imprint","IMPRINT",FACE,{"disambiguationData":[TD([[makeQuery(id+"F5.imprint","IMPRINT",EDGE,{"derivedFrom":sQuery(id+"F5.wireOp",EDGE,"E12.1.1.1")}),-1.0]])]});
            var Q49;
            {var subQ0=sQuery(id+"F5.wireOp",EDGE,"E12.0.2.2");var subQ1=sQuery(id+"F5.wireOp",EDGE,"E12.0.1.4");var subQ2=makeQuery(id+"F5.imprint","INTERSECT",VERTEX,{"derivedFrom":[subQ1,subQ0]});Q49=makeQuery(id+"F5.imprint","IMPRINT",FACE,{"disambiguationData":[TD([[makeQuery(id+"F5.imprint","IMPRINT",EDGE,{"disambiguationData":[TD([[subQ2,-1.0]])],"derivedFrom":subQ1}),-1.0]])]});}
            var Q50;
            Q50=makeQuery(id+"F5.imprint","IMPRINT",FACE,{"disambiguationData":[TD([[makeQuery(id+"F5.imprint","IMPRINT",EDGE,{"derivedFrom":sQuery(id+"F5.wireOp",EDGE,"E12.1.2.1")}),-1.0]])]});
            var Q51;
            {var subQ0=sQuery(id+"F5.wireOp",EDGE,"E12.1.2.2");var subQ1=sQuery(id+"F5.wireOp",EDGE,"E12.1.1.4");var subQ2=makeQuery(id+"F5.imprint","INTERSECT",VERTEX,{"derivedFrom":[subQ1,subQ0]});Q51=makeQuery(id+"F5.imprint","IMPRINT",FACE,{"disambiguationData":[TD([[makeQuery(id+"F5.imprint","IMPRINT",EDGE,{"disambiguationData":[TD([[subQ2,-1.0]])],"derivedFrom":subQ1}),-1.0]])]});}
            var Q52;
            Q52=makeQuery(id+"F5.imprint","IMPRINT",FACE,{"disambiguationData":[TD([[makeQuery(id+"F5.imprint","IMPRINT",EDGE,{"derivedFrom":sQuery(id+"F5.wireOp",EDGE,"E12.2.1.1")}),-1.0]])]});
            var Q53;
            {var subQ0=sQuery(id+"F5.wireOp",EDGE,"E12.2.1.2");var subQ1=sQuery(id+"F5.wireOp",EDGE,"E12.2.0.4");var subQ2=makeQuery(id+"F5.imprint","INTERSECT",VERTEX,{"derivedFrom":[subQ1,subQ0]});Q53=makeQuery(id+"F5.imprint","IMPRINT",FACE,{"disambiguationData":[TD([[makeQuery(id+"F5.imprint","IMPRINT",EDGE,{"disambiguationData":[TD([[subQ2,-1.0]])],"derivedFrom":subQ1}),-1.0]])]});}
            var Q54;
            {var subQ0=sQuery(id+"F5.wireOp",EDGE,"E12.3.1.2");var subQ1=sQuery(id+"F5.wireOp",EDGE,"E12.3.0.4");var subQ2=makeQuery(id+"F5.imprint","INTERSECT",VERTEX,{"derivedFrom":[subQ1,subQ0]});Q54=makeQuery(id+"F5.imprint","IMPRINT",FACE,{"disambiguationData":[TD([[makeQuery(id+"F5.imprint","IMPRINT",EDGE,{"disambiguationData":[TD([[subQ2,-1.0]])],"derivedFrom":subQ1}),-1.0]])]});}
            var Q55;
            Q55=makeQuery(id+"F5.imprint","IMPRINT",FACE,{"disambiguationData":[TD([[makeQuery(id+"F5.imprint","IMPRINT",EDGE,{"derivedFrom":sQuery(id+"F5.wireOp",EDGE,"E12.3.1.1")}),-1.0]])]});
            var Q56;
            {var subQ0=sQuery(id+"F5.wireOp",EDGE,"E12.2.2.2");var subQ1=sQuery(id+"F5.wireOp",EDGE,"E12.2.1.4");var subQ2=makeQuery(id+"F5.imprint","INTERSECT",VERTEX,{"derivedFrom":[subQ1,subQ0]});Q56=makeQuery(id+"F5.imprint","IMPRINT",FACE,{"disambiguationData":[TD([[makeQuery(id+"F5.imprint","IMPRINT",EDGE,{"disambiguationData":[TD([[subQ2,-1.0]])],"derivedFrom":subQ1}),-1.0]])]});}
            var Q57;
            Q57=makeQuery(id+"F5.imprint","IMPRINT",FACE,{"disambiguationData":[TD([[makeQuery(id+"F5.imprint","IMPRINT",EDGE,{"derivedFrom":sQuery(id+"F5.wireOp",EDGE,"E12.2.2.1")}),-1.0]])]});
            var Q58;
            {var subQ0=sQuery(id+"F5.wireOp",EDGE,"E12.1.3.2");var subQ1=sQuery(id+"F5.wireOp",EDGE,"E12.1.2.4");var subQ2=makeQuery(id+"F5.imprint","INTERSECT",VERTEX,{"derivedFrom":[subQ1,subQ0]});Q58=makeQuery(id+"F5.imprint","IMPRINT",FACE,{"disambiguationData":[TD([[makeQuery(id+"F5.imprint","IMPRINT",EDGE,{"disambiguationData":[TD([[subQ2,-1.0]])],"derivedFrom":subQ1}),-1.0]])]});}
            var Q59;
            Q59=makeQuery(id+"F5.imprint","IMPRINT",FACE,{"disambiguationData":[TD([[makeQuery(id+"F5.imprint","IMPRINT",EDGE,{"derivedFrom":sQuery(id+"F5.wireOp",EDGE,"E12.1.3.1")}),-1.0]])]});
            var Q60;
            {var subQ0=sQuery(id+"F5.wireOp",EDGE,"E12.0.4.2");var subQ1=sQuery(id+"F5.wireOp",EDGE,"E12.0.3.4");var subQ2=makeQuery(id+"F5.imprint","INTERSECT",VERTEX,{"derivedFrom":[subQ1,subQ0]});Q60=makeQuery(id+"F5.imprint","IMPRINT",FACE,{"disambiguationData":[TD([[makeQuery(id+"F5.imprint","IMPRINT",EDGE,{"disambiguationData":[TD([[subQ2,-1.0]])],"derivedFrom":subQ1}),-1.0]])]});}
            var Q61;
            {var subQ0=sQuery(id+"F5.wireOp",EDGE,"E12.1.4.2");var subQ1=sQuery(id+"F5.wireOp",EDGE,"E12.1.3.4");var subQ2=makeQuery(id+"F5.imprint","INTERSECT",VERTEX,{"derivedFrom":[subQ1,subQ0]});Q61=makeQuery(id+"F5.imprint","IMPRINT",FACE,{"disambiguationData":[TD([[makeQuery(id+"F5.imprint","IMPRINT",EDGE,{"disambiguationData":[TD([[subQ2,-1.0]])],"derivedFrom":subQ1}),-1.0]])]});}
            var Q62;
            Q62=makeQuery(id+"F5.imprint","IMPRINT",FACE,{"disambiguationData":[TD([[makeQuery(id+"F5.imprint","IMPRINT",EDGE,{"derivedFrom":sQuery(id+"F5.wireOp",EDGE,"E12.2.3.1")}),-1.0]])]});
            var Q63;
            {var subQ0=sQuery(id+"F5.wireOp",EDGE,"E12.2.3.2");var subQ1=sQuery(id+"F5.wireOp",EDGE,"E12.2.2.4");var subQ2=makeQuery(id+"F5.imprint","INTERSECT",VERTEX,{"derivedFrom":[subQ1,subQ0]});Q63=makeQuery(id+"F5.imprint","IMPRINT",FACE,{"disambiguationData":[TD([[makeQuery(id+"F5.imprint","IMPRINT",EDGE,{"disambiguationData":[TD([[subQ2,-1.0]])],"derivedFrom":subQ1}),-1.0]])]});}
            var Q64;
            Q64=makeQuery(id+"F5.imprint","IMPRINT",FACE,{"disambiguationData":[TD([[makeQuery(id+"F5.imprint","IMPRINT",EDGE,{"derivedFrom":sQuery(id+"F5.wireOp",EDGE,"E12.3.3.1")}),-1.0]])]});
            var Q65;
            {var subQ0=sQuery(id+"F5.wireOp",EDGE,"E12.2.4.2");var subQ1=sQuery(id+"F5.wireOp",EDGE,"E12.2.3.4");var subQ2=makeQuery(id+"F5.imprint","INTERSECT",VERTEX,{"derivedFrom":[subQ1,subQ0]});Q65=makeQuery(id+"F5.imprint","IMPRINT",FACE,{"disambiguationData":[TD([[makeQuery(id+"F5.imprint","IMPRINT",EDGE,{"disambiguationData":[TD([[subQ2,-1.0]])],"derivedFrom":subQ1}),-1.0]])]});}
            var Q66;
            {var subQ0=sQuery(id+"F5.wireOp",EDGE,"E12.3.4.2");var subQ1=sQuery(id+"F5.wireOp",EDGE,"E12.3.3.4");var subQ2=makeQuery(id+"F5.imprint","INTERSECT",VERTEX,{"derivedFrom":[subQ1,subQ0]});Q66=makeQuery(id+"F5.imprint","IMPRINT",FACE,{"disambiguationData":[TD([[makeQuery(id+"F5.imprint","IMPRINT",EDGE,{"disambiguationData":[TD([[subQ2,-1.0]])],"derivedFrom":subQ1}),-1.0]])]});}
            var Q67;
            {var subQ0=sQuery(id+"F5.wireOp",EDGE,"E12.4.4.2");var subQ1=sQuery(id+"F5.wireOp",EDGE,"E12.4.3.4");var subQ2=makeQuery(id+"F5.imprint","INTERSECT",VERTEX,{"derivedFrom":[subQ1,subQ0]});Q67=makeQuery(id+"F5.imprint","IMPRINT",FACE,{"disambiguationData":[TD([[makeQuery(id+"F5.imprint","IMPRINT",EDGE,{"disambiguationData":[TD([[subQ2,-1.0]])],"derivedFrom":subQ1}),-1.0]])]});}
            var Q68;
            {var subQ0=sQuery(id+"F5.wireOp",EDGE,"E12.5.4.2");var subQ1=sQuery(id+"F5.wireOp",EDGE,"E12.5.3.4");var subQ2=makeQuery(id+"F5.imprint","INTERSECT",VERTEX,{"derivedFrom":[subQ1,subQ0]});Q68=makeQuery(id+"F5.imprint","IMPRINT",FACE,{"disambiguationData":[TD([[makeQuery(id+"F5.imprint","IMPRINT",EDGE,{"disambiguationData":[TD([[subQ2,-1.0]])],"derivedFrom":subQ1}),-1.0]])]});}
            var Q69;
            {var subQ0=sQuery(id+"F5.wireOp",EDGE,"E12.6.4.2");var subQ1=sQuery(id+"F5.wireOp",EDGE,"E12.6.3.4");var subQ2=makeQuery(id+"F5.imprint","INTERSECT",VERTEX,{"derivedFrom":[subQ1,subQ0]});Q69=makeQuery(id+"F5.imprint","IMPRINT",FACE,{"disambiguationData":[TD([[makeQuery(id+"F5.imprint","IMPRINT",EDGE,{"disambiguationData":[TD([[subQ2,-1.0]])],"derivedFrom":subQ1}),-1.0]])]});}
            var Q70;
            {var subQ0=sQuery(id+"F5.wireOp",EDGE,"E12.7.4.2");var subQ1=sQuery(id+"F5.wireOp",EDGE,"E12.7.3.4");var subQ2=makeQuery(id+"F5.imprint","INTERSECT",VERTEX,{"derivedFrom":[subQ1,subQ0]});Q70=makeQuery(id+"F5.imprint","IMPRINT",FACE,{"disambiguationData":[TD([[makeQuery(id+"F5.imprint","IMPRINT",EDGE,{"disambiguationData":[TD([[subQ2,-1.0]])],"derivedFrom":subQ1}),-1.0]])]});}
            var Q71;
            {var subQ0=sQuery(id+"F5.wireOp",EDGE,"E12.8.4.2");var subQ1=sQuery(id+"F5.wireOp",EDGE,"E12.8.3.4");var subQ2=makeQuery(id+"F5.imprint","INTERSECT",VERTEX,{"derivedFrom":[subQ1,subQ0]});Q71=makeQuery(id+"F5.imprint","IMPRINT",FACE,{"disambiguationData":[TD([[makeQuery(id+"F5.imprint","IMPRINT",EDGE,{"disambiguationData":[TD([[subQ2,-1.0]])],"derivedFrom":subQ1}),-1.0]])]});}
            var Q72;
            {var subQ0=sQuery(id+"F5.wireOp",EDGE,"E12.9.4.2");var subQ1=sQuery(id+"F5.wireOp",EDGE,"E12.9.3.4");var subQ2=makeQuery(id+"F5.imprint","INTERSECT",VERTEX,{"derivedFrom":[subQ1,subQ0]});Q72=makeQuery(id+"F5.imprint","IMPRINT",FACE,{"disambiguationData":[TD([[makeQuery(id+"F5.imprint","IMPRINT",EDGE,{"disambiguationData":[TD([[subQ2,-1.0]])],"derivedFrom":subQ1}),-1.0]])]});}
            var Q73;
            Q73=makeQuery(id+"F5.imprint","IMPRINT",FACE,{"disambiguationData":[TD([[makeQuery(id+"F5.imprint","IMPRINT",EDGE,{"derivedFrom":sQuery(id+"F5.wireOp",EDGE,"E12.10.3.1")}),-1.0]])]});
            var Q74;
            Q74=makeQuery(id+"F5.imprint","IMPRINT",FACE,{"disambiguationData":[TD([[makeQuery(id+"F5.imprint","IMPRINT",EDGE,{"derivedFrom":sQuery(id+"F5.wireOp",EDGE,"E12.10.2.1")}),-1.0]])]});
            var Q75;
            Q75=makeQuery(id+"F5.imprint","IMPRINT",FACE,{"disambiguationData":[TD([[makeQuery(id+"F5.imprint","IMPRINT",EDGE,{"derivedFrom":sQuery(id+"F5.wireOp",EDGE,"E12.10.1.1")}),-1.0]])]});
            var Q76;
            {var subQ0=sQuery(id+"F5.wireOp",EDGE,"E12.9.1.2");var subQ1=sQuery(id+"F5.wireOp",EDGE,"E12.9.0.4");var subQ2=makeQuery(id+"F5.imprint","INTERSECT",VERTEX,{"derivedFrom":[subQ1,subQ0]});Q76=makeQuery(id+"F5.imprint","IMPRINT",FACE,{"disambiguationData":[TD([[makeQuery(id+"F5.imprint","IMPRINT",EDGE,{"disambiguationData":[TD([[subQ2,-1.0]])],"derivedFrom":subQ1}),-1.0]])]});}
            var Q77;
            {var subQ0=sQuery(id+"F5.wireOp",EDGE,"E12.9.2.2");var subQ1=sQuery(id+"F5.wireOp",EDGE,"E12.9.1.4");var subQ2=makeQuery(id+"F5.imprint","INTERSECT",VERTEX,{"derivedFrom":[subQ1,subQ0]});Q77=makeQuery(id+"F5.imprint","IMPRINT",FACE,{"disambiguationData":[TD([[makeQuery(id+"F5.imprint","IMPRINT",EDGE,{"disambiguationData":[TD([[subQ2,-1.0]])],"derivedFrom":subQ1}),-1.0]])]});}
            var Q78;
            {var subQ0=sQuery(id+"F5.wireOp",EDGE,"E12.8.1.2");var subQ1=sQuery(id+"F5.wireOp",EDGE,"E12.8.0.4");var subQ2=makeQuery(id+"F5.imprint","INTERSECT",VERTEX,{"derivedFrom":[subQ1,subQ0]});Q78=makeQuery(id+"F5.imprint","IMPRINT",FACE,{"disambiguationData":[TD([[makeQuery(id+"F5.imprint","IMPRINT",EDGE,{"disambiguationData":[TD([[subQ2,-1.0]])],"derivedFrom":subQ1}),-1.0]])]});}
            var Q79;
            Q79=makeQuery(id+"F5.imprint","IMPRINT",FACE,{"disambiguationData":[TD([[makeQuery(id+"F5.imprint","IMPRINT",EDGE,{"derivedFrom":sQuery(id+"F5.wireOp",EDGE,"E12.9.1.1")}),-1.0]])]});
            var Q80;
            Q80=makeQuery(id+"F5.imprint","IMPRINT",FACE,{"disambiguationData":[TD([[makeQuery(id+"F5.imprint","IMPRINT",EDGE,{"derivedFrom":sQuery(id+"F5.wireOp",EDGE,"E12.9.2.1")}),-1.0]])]});
            var Q81;
            {var subQ0=sQuery(id+"F5.wireOp",EDGE,"E12.9.3.2");var subQ1=sQuery(id+"F5.wireOp",EDGE,"E12.9.2.4");var subQ2=makeQuery(id+"F5.imprint","INTERSECT",VERTEX,{"derivedFrom":[subQ1,subQ0]});Q81=makeQuery(id+"F5.imprint","IMPRINT",FACE,{"disambiguationData":[TD([[makeQuery(id+"F5.imprint","IMPRINT",EDGE,{"disambiguationData":[TD([[subQ2,-1.0]])],"derivedFrom":subQ1}),-1.0]])]});}
            var Q82;
            Q82=makeQuery(id+"F5.imprint","IMPRINT",FACE,{"disambiguationData":[TD([[makeQuery(id+"F5.imprint","IMPRINT",EDGE,{"derivedFrom":sQuery(id+"F5.wireOp",EDGE,"E12.9.3.1")}),-1.0]])]});
            var Q83;
            {var subQ0=sQuery(id+"F5.wireOp",EDGE,"E12.8.3.2");var subQ1=sQuery(id+"F5.wireOp",EDGE,"E12.8.2.4");var subQ2=makeQuery(id+"F5.imprint","INTERSECT",VERTEX,{"derivedFrom":[subQ1,subQ0]});Q83=makeQuery(id+"F5.imprint","IMPRINT",FACE,{"disambiguationData":[TD([[makeQuery(id+"F5.imprint","IMPRINT",EDGE,{"disambiguationData":[TD([[subQ2,-1.0]])],"derivedFrom":subQ1}),-1.0]])]});}
            var Q84;
            {var subQ0=sQuery(id+"F5.wireOp",EDGE,"E12.8.2.2");var subQ1=sQuery(id+"F5.wireOp",EDGE,"E12.8.1.4");var subQ2=makeQuery(id+"F5.imprint","INTERSECT",VERTEX,{"derivedFrom":[subQ1,subQ0]});Q84=makeQuery(id+"F5.imprint","IMPRINT",FACE,{"disambiguationData":[TD([[makeQuery(id+"F5.imprint","IMPRINT",EDGE,{"disambiguationData":[TD([[subQ2,-1.0]])],"derivedFrom":subQ1}),-1.0]])]});}
            var Q85;
            Q85=makeQuery(id+"F5.imprint","IMPRINT",FACE,{"disambiguationData":[TD([[makeQuery(id+"F5.imprint","IMPRINT",EDGE,{"derivedFrom":sQuery(id+"F5.wireOp",EDGE,"E12.8.1.1")}),-1.0]])]});
            var Q86;
            {var subQ0=sQuery(id+"F5.wireOp",EDGE,"E12.7.1.2");var subQ1=sQuery(id+"F5.wireOp",EDGE,"E12.7.0.4");var subQ2=makeQuery(id+"F5.imprint","INTERSECT",VERTEX,{"derivedFrom":[subQ1,subQ0]});Q86=makeQuery(id+"F5.imprint","IMPRINT",FACE,{"disambiguationData":[TD([[makeQuery(id+"F5.imprint","IMPRINT",EDGE,{"disambiguationData":[TD([[subQ2,-1.0]])],"derivedFrom":subQ1}),-1.0]])]});}
            var Q87;
            Q87=makeQuery(id+"F5.imprint","IMPRINT",FACE,{"disambiguationData":[TD([[makeQuery(id+"F5.imprint","IMPRINT",EDGE,{"derivedFrom":sQuery(id+"F5.wireOp",EDGE,"E12.7.1.1")}),-1.0]])]});
            var Q88;
            {var subQ0=sQuery(id+"F5.wireOp",EDGE,"E12.6.1.2");var subQ1=sQuery(id+"F5.wireOp",EDGE,"E12.6.0.4");var subQ2=makeQuery(id+"F5.imprint","INTERSECT",VERTEX,{"derivedFrom":[subQ1,subQ0]});Q88=makeQuery(id+"F5.imprint","IMPRINT",FACE,{"disambiguationData":[TD([[makeQuery(id+"F5.imprint","IMPRINT",EDGE,{"disambiguationData":[TD([[subQ2,-1.0]])],"derivedFrom":subQ1}),-1.0]])]});}
            var Q89;
            Q89=makeQuery(id+"F5.imprint","IMPRINT",FACE,{"disambiguationData":[TD([[makeQuery(id+"F5.imprint","IMPRINT",EDGE,{"derivedFrom":sQuery(id+"F5.wireOp",EDGE,"E12.6.1.1")}),-1.0]])]});
            var Q90;
            {var subQ0=sQuery(id+"F5.wireOp",EDGE,"E12.5.1.2");var subQ1=sQuery(id+"F5.wireOp",EDGE,"E12.5.0.4");var subQ2=makeQuery(id+"F5.imprint","INTERSECT",VERTEX,{"derivedFrom":[subQ1,subQ0]});Q90=makeQuery(id+"F5.imprint","IMPRINT",FACE,{"disambiguationData":[TD([[makeQuery(id+"F5.imprint","IMPRINT",EDGE,{"disambiguationData":[TD([[subQ2,-1.0]])],"derivedFrom":subQ1}),-1.0]])]});}
            var Q91;
            {var subQ0=sQuery(id+"F5.wireOp",EDGE,"E12.4.1.2");var subQ1=sQuery(id+"F5.wireOp",EDGE,"E12.4.0.4");var subQ2=makeQuery(id+"F5.imprint","INTERSECT",VERTEX,{"derivedFrom":[subQ1,subQ0]});Q91=makeQuery(id+"F5.imprint","IMPRINT",FACE,{"disambiguationData":[TD([[makeQuery(id+"F5.imprint","IMPRINT",EDGE,{"disambiguationData":[TD([[subQ2,-1.0]])],"derivedFrom":subQ1}),-1.0]])]});}
            var Q92;
            Q92=makeQuery(id+"F5.imprint","IMPRINT",FACE,{"disambiguationData":[TD([[makeQuery(id+"F5.imprint","IMPRINT",EDGE,{"derivedFrom":sQuery(id+"F5.wireOp",EDGE,"E12.5.1.1")}),-1.0]])]});
            var Q93;
            {var subQ0=sQuery(id+"F5.wireOp",EDGE,"E12.4.2.2");var subQ1=sQuery(id+"F5.wireOp",EDGE,"E12.4.1.4");var subQ2=makeQuery(id+"F5.imprint","INTERSECT",VERTEX,{"derivedFrom":[subQ1,subQ0]});Q93=makeQuery(id+"F5.imprint","IMPRINT",FACE,{"disambiguationData":[TD([[makeQuery(id+"F5.imprint","IMPRINT",EDGE,{"disambiguationData":[TD([[subQ2,-1.0]])],"derivedFrom":subQ1}),-1.0]])]});}
            var Q94;
            Q94=makeQuery(id+"F5.imprint","IMPRINT",FACE,{"disambiguationData":[TD([[makeQuery(id+"F5.imprint","IMPRINT",EDGE,{"derivedFrom":sQuery(id+"F5.wireOp",EDGE,"E12.5.2.1")}),-1.0]])]});
            var Q95;
            {var subQ0=sQuery(id+"F5.wireOp",EDGE,"E12.5.3.2");var subQ1=sQuery(id+"F5.wireOp",EDGE,"E12.5.2.4");var subQ2=makeQuery(id+"F5.imprint","INTERSECT",VERTEX,{"derivedFrom":[subQ1,subQ0]});Q95=makeQuery(id+"F5.imprint","IMPRINT",FACE,{"disambiguationData":[TD([[makeQuery(id+"F5.imprint","IMPRINT",EDGE,{"disambiguationData":[TD([[subQ2,-1.0]])],"derivedFrom":subQ1}),-1.0]])]});}
            var Q96;
            Q96=makeQuery(id+"F5.imprint","IMPRINT",FACE,{"disambiguationData":[TD([[makeQuery(id+"F5.imprint","IMPRINT",EDGE,{"derivedFrom":sQuery(id+"F5.wireOp",EDGE,"E12.6.3.1")}),-1.0]])]});
            var Q97;
            {var subQ0=sQuery(id+"F5.wireOp",EDGE,"E12.6.3.2");var subQ1=sQuery(id+"F5.wireOp",EDGE,"E12.6.2.4");var subQ2=makeQuery(id+"F5.imprint","INTERSECT",VERTEX,{"derivedFrom":[subQ1,subQ0]});Q97=makeQuery(id+"F5.imprint","IMPRINT",FACE,{"disambiguationData":[TD([[makeQuery(id+"F5.imprint","IMPRINT",EDGE,{"disambiguationData":[TD([[subQ2,-1.0]])],"derivedFrom":subQ1}),-1.0]])]});}
            var Q98;
            Q98=makeQuery(id+"F5.imprint","IMPRINT",FACE,{"disambiguationData":[TD([[makeQuery(id+"F5.imprint","IMPRINT",EDGE,{"derivedFrom":sQuery(id+"F5.wireOp",EDGE,"E12.6.2.1")}),-1.0]])]});
            var Q99;
            {var subQ0=sQuery(id+"F5.wireOp",EDGE,"E12.5.2.2");var subQ1=sQuery(id+"F5.wireOp",EDGE,"E12.5.1.4");var subQ2=makeQuery(id+"F5.imprint","INTERSECT",VERTEX,{"derivedFrom":[subQ1,subQ0]});Q99=makeQuery(id+"F5.imprint","IMPRINT",FACE,{"disambiguationData":[TD([[makeQuery(id+"F5.imprint","IMPRINT",EDGE,{"disambiguationData":[TD([[subQ2,-1.0]])],"derivedFrom":subQ1}),-1.0]])]});}
            var Q100;
            {var subQ0=sQuery(id+"F5.wireOp",EDGE,"E12.6.2.2");var subQ1=sQuery(id+"F5.wireOp",EDGE,"E12.6.1.4");var subQ2=makeQuery(id+"F5.imprint","INTERSECT",VERTEX,{"derivedFrom":[subQ1,subQ0]});Q100=makeQuery(id+"F5.imprint","IMPRINT",FACE,{"disambiguationData":[TD([[makeQuery(id+"F5.imprint","IMPRINT",EDGE,{"disambiguationData":[TD([[subQ2,-1.0]])],"derivedFrom":subQ1}),-1.0]])]});}
            var Q101;
            Q101=makeQuery(id+"F5.imprint","IMPRINT",FACE,{"disambiguationData":[TD([[makeQuery(id+"F5.imprint","IMPRINT",EDGE,{"derivedFrom":sQuery(id+"F5.wireOp",EDGE,"E12.7.2.1")}),-1.0]])]});
            var Q102;
            {var subQ0=sQuery(id+"F5.wireOp",EDGE,"E12.7.3.2");var subQ1=sQuery(id+"F5.wireOp",EDGE,"E12.7.2.4");var subQ2=makeQuery(id+"F5.imprint","INTERSECT",VERTEX,{"derivedFrom":[subQ1,subQ0]});Q102=makeQuery(id+"F5.imprint","IMPRINT",FACE,{"disambiguationData":[TD([[makeQuery(id+"F5.imprint","IMPRINT",EDGE,{"disambiguationData":[TD([[subQ2,-1.0]])],"derivedFrom":subQ1}),-1.0]])]});}
            var Q103;
            Q103=makeQuery(id+"F5.imprint","IMPRINT",FACE,{"disambiguationData":[TD([[makeQuery(id+"F5.imprint","IMPRINT",EDGE,{"derivedFrom":sQuery(id+"F5.wireOp",EDGE,"E12.8.3.1")}),-1.0]])]});
            var Q104;
            Q104=makeQuery(id+"F5.imprint","IMPRINT",FACE,{"disambiguationData":[TD([[makeQuery(id+"F5.imprint","IMPRINT",EDGE,{"derivedFrom":sQuery(id+"F5.wireOp",EDGE,"E12.7.3.1")}),-1.0]])]});
            var Q105;
            Q105=makeQuery(id+"F5.imprint","IMPRINT",FACE,{"disambiguationData":[TD([[makeQuery(id+"F5.imprint","IMPRINT",EDGE,{"derivedFrom":sQuery(id+"F5.wireOp",EDGE,"E12.8.2.1")}),-1.0]])]});
            var Q106;
            {var subQ0=sQuery(id+"F5.wireOp",EDGE,"E12.7.2.2");var subQ1=sQuery(id+"F5.wireOp",EDGE,"E12.7.1.4");var subQ2=makeQuery(id+"F5.imprint","INTERSECT",VERTEX,{"derivedFrom":[subQ1,subQ0]});Q106=makeQuery(id+"F5.imprint","IMPRINT",FACE,{"disambiguationData":[TD([[makeQuery(id+"F5.imprint","IMPRINT",EDGE,{"disambiguationData":[TD([[subQ2,-1.0]])],"derivedFrom":subQ1}),-1.0]])]});}
            var Q107;
            Q107=makeQuery(id+"F5.imprint","IMPRINT",FACE,{"disambiguationData":[TD([[makeQuery(id+"F5.imprint","IMPRINT",EDGE,{"derivedFrom":sQuery(id+"F5.wireOp",EDGE,"E12.4.1.1")}),-1.0]])]});
            var Q108;
            {var subQ0=sQuery(id+"F5.wireOp",EDGE,"E12.3.2.2");var subQ1=sQuery(id+"F5.wireOp",EDGE,"E12.3.1.4");var subQ2=makeQuery(id+"F5.imprint","INTERSECT",VERTEX,{"derivedFrom":[subQ1,subQ0]});Q108=makeQuery(id+"F5.imprint","IMPRINT",FACE,{"disambiguationData":[TD([[makeQuery(id+"F5.imprint","IMPRINT",EDGE,{"disambiguationData":[TD([[subQ2,-1.0]])],"derivedFrom":subQ1}),-1.0]])]});}
            var Q109;
            Q109=makeQuery(id+"F5.imprint","IMPRINT",FACE,{"disambiguationData":[TD([[makeQuery(id+"F5.imprint","IMPRINT",EDGE,{"derivedFrom":sQuery(id+"F5.wireOp",EDGE,"E12.3.2.1")}),-1.0]])]});
            var Q110;
            {var subQ0=sQuery(id+"F5.wireOp",EDGE,"E12.3.3.2");var subQ1=sQuery(id+"F5.wireOp",EDGE,"E12.3.2.4");var subQ2=makeQuery(id+"F5.imprint","INTERSECT",VERTEX,{"derivedFrom":[subQ1,subQ0]});Q110=makeQuery(id+"F5.imprint","IMPRINT",FACE,{"disambiguationData":[TD([[makeQuery(id+"F5.imprint","IMPRINT",EDGE,{"disambiguationData":[TD([[subQ2,-1.0]])],"derivedFrom":subQ1}),-1.0]])]});}
            var Q111;
            Q111=makeQuery(id+"F5.imprint","IMPRINT",FACE,{"disambiguationData":[TD([[makeQuery(id+"F5.imprint","IMPRINT",EDGE,{"derivedFrom":sQuery(id+"F5.wireOp",EDGE,"E12.4.2.1")}),-1.0]])]});
            var Q112;
            {var subQ0=sQuery(id+"F5.wireOp",EDGE,"E12.4.3.2");var subQ1=sQuery(id+"F5.wireOp",EDGE,"E12.4.2.4");var subQ2=makeQuery(id+"F5.imprint","INTERSECT",VERTEX,{"derivedFrom":[subQ1,subQ0]});Q112=makeQuery(id+"F5.imprint","IMPRINT",FACE,{"disambiguationData":[TD([[makeQuery(id+"F5.imprint","IMPRINT",EDGE,{"disambiguationData":[TD([[subQ2,-1.0]])],"derivedFrom":subQ1}),-1.0]])]});}
            var Q113;
            Q113=makeQuery(id+"F5.imprint","IMPRINT",FACE,{"disambiguationData":[TD([[makeQuery(id+"F5.imprint","IMPRINT",EDGE,{"derivedFrom":sQuery(id+"F5.wireOp",EDGE,"E12.5.3.1")}),-1.0]])]});
            var Q114;
            Q114=makeQuery(id+"F5.imprint","IMPRINT",FACE,{"disambiguationData":[TD([[makeQuery(id+"F5.imprint","IMPRINT",EDGE,{"derivedFrom":sQuery(id+"F5.wireOp",EDGE,"E12.4.3.1")}),-1.0]])]});
            extrude(context, id + "F6", {"entities" : qUnion([Q0, Q1, Q2, Q3, Q4, Q5, Q6, Q7, Q8, Q9, Q10, Q11, Q12, Q13, Q14, Q15, Q16, Q17, Q18, Q19, Q20, Q21, Q22, Q23, Q24, Q25, Q26, Q27, Q28, Q29, Q30, Q31, Q32, Q33, Q34, Q35, Q36, Q37, Q38, Q39, Q40, Q41, Q42, Q43, Q44, Q45, Q46, Q47, Q48, Q49, Q50, Q51, Q52, Q53, Q54, Q55, Q56, Q57, Q58, Q59, Q60, Q61, Q62, Q63, Q64, Q65, Q66, Q67, Q68, Q69, Q70, Q71, Q72, Q73, Q74, Q75, Q76, Q77, Q78, Q79, Q80, Q81, Q82, Q83, Q84, Q85, Q86, Q87, Q88, Q89, Q90, Q91, Q92, Q93, Q94, Q95, Q96, Q97, Q98, Q99, Q100, Q101, Q102, Q103, Q104, Q105, Q106, Q107, Q108, Q109, Q110, Q111, Q112, Q113, Q114]), "operationType" : NewBodyOperationType.REMOVE, "oppositeDirection" : true, "depth" : 3 * mm, "offsetDistance" : 25 * mm});
        }
        {
            var Q0;
            Q0 = qSketchRegion(id + "F0", true);
            extrude(context, id + "F7", {"entities" : qUnion([Q0]), "operationType" : NewBodyOperationType.ADD, "depth" : 5 * mm, "offsetDistance" : 25 * mm, "hasSecondDirection" : true, "secondDirectionOppositeDirection" : true, "secondDirectionDepth" : 3 * mm});
        }
        {
            var Q0;
            Q0=makeQuery(id+"F2.opExtrude","SWEPT_FACE",FACE,{"disambiguationData":[OSD([sQuery(id+"F1.wireOp",EDGE,"E1.top")])]});
            var sketch = newSketch(context, id + "F8", { "sketchPlane" : qUnion([Q0])});
            skText(sketch, "E13", { "text": "GRILL-EAT-SHIT-REPEAT", "fontName": "OpenSans-Regular.ttf"});
            const initialGuessF8  = {"E13": [-0.0629, -0.00719, 1, 0, 0.0081]};
            skSetInitialGuess(sketch, initialGuessF8);
            skSolve(sketch);
        }
        {
            var Q0;
            Q0 = qSketchRegion(id + "F8", true);
            extrude(context, id + "F9", {"entities" : qUnion([Q0]), "operationType" : NewBodyOperationType.REMOVE, "oppositeDirection" : true, "depth" : 2 * mm, "offsetDistance" : 25 * mm});
        }
        {
            var Q0;
            Q0=makeQuery(id+"F2.opExtrude","CAP_FACE",FACE,{"disambiguationData":[OSD([sQuery(id+"F1.wireOp",EDGE,"E1.bottom"),sQuery(id+"F1.wireOp",EDGE,"E1.top"),sQuery(id+"F1.wireOp",EDGE,"E1.left"),sQuery(id+"F1.wireOp",EDGE,"E1.right"),sQuery(id+"F1.wireOp",EDGE,"E2.filletArc"),sQuery(id+"F1.wireOp",EDGE,"E3.filletArc"),sQuery(id+"F1.wireOp",EDGE,"E4.filletArc"),sQuery(id+"F1.wireOp",EDGE,"E5.filletArc")])],"isStart":false});
            var sketch = newSketch(context, id + "F10", { "sketchPlane" : qUnion([Q0])});
            skText(sketch, "E14", { "text": "\'Dont go chasing waterfalls\'\n- TLC\n\n06.05.17", "fontName": "OpenSans-Regular.ttf"});
            const initialGuessF10  = {"E14": [-0.06239, 0.0101, 1, 0, 0.00669]};
            skSetInitialGuess(sketch, initialGuessF10);
            skSolve(sketch);
        }
        {
            var Q0;
            Q0 = qSketchRegion(id + "F10", true);
            extrude(context, id + "F11", {"entities" : qUnion([Q0]), "operationType" : NewBodyOperationType.REMOVE, "oppositeDirection" : true, "depth" : 2 * mm, "offsetDistance" : 25 * mm});
        }
        {
            var Q0;
            Q0=makeQuery(id+"F2.opExtrude","SWEPT_FACE",FACE,{"disambiguationData":[OSD([sQuery(id+"F1.wireOp",EDGE,"E1.bottom")])]});
            var sketch = newSketch(context, id + "F12", { "sketchPlane" : qUnion([Q0])});
            skLineSegment(sketch, "E15.bottom", {"start": v(-57.16, -7.18) * mm, "end": v(57.63, -7.18) * mm});
            skLineSegment(sketch, "E15.top", {"start": v(-52.16, 2.24) * mm, "end": v(48.63, 2.24) * mm});
            skLineSegment(sketch, "E15.left", {"start": v(-57.16, -7.18) * mm, "end": v(-57.16, -2.76) * mm});
            skLineSegment(sketch, "E15.right", {"start": v(57.63, -7.18) * mm, "end": v(57.63, -6.76) * mm});
            skPoint(sketch, "E16.visualSharp", {"position": v(-57.16, 2.24) * mm});
            skArc(sketch, "E16.filletArc", {"start": v(-52.16, 2.24) * mm, "mid": v(-55.7, 0.78) * mm, "end": v(-57.16, -2.76) * mm});
            skPoint(sketch, "E17.visualSharp", {"position": v(57.63, 2.24) * mm});
            skArc(sketch, "E17.filletArc", {"start": v(57.63, -6.76) * mm, "mid": v(55, -0.4) * mm, "end": v(48.63, 2.24) * mm});
            skSolve(sketch);
        }
        {
            var Q0;
            Q0=makeQuery(id+"F12.imprint","IMPRINT",FACE,{"disambiguationData":[TD([[makeQuery(id+"F12.imprint","IMPRINT",EDGE,{"derivedFrom":sQuery(id+"F12.wireOp",EDGE,"E15.bottom")}),1.0]])]});
            extrude(context, id + "F13", {"entities" : qUnion([Q0]), "operationType" : NewBodyOperationType.REMOVE, "endBound" : BoundingType.SYMMETRIC, "oppositeDirection" : true, "depth" : 4 * mm, "offsetDistance" : 25 * mm, "hasDraft" : true, "draftAngle" : 20 * degree, "draftPullDirection" : true});
        }
    });
